FCSTD DOCUMENT  (FreeCAD 0.20R29177 (Git))
Label: FaceAr10Portrait
License: All rights reserved
LicenseURL: http://en.wikipedia.org/wiki/All_rights_reserved
objects: Sketcher::SketchObject×1, PartDesign::Body×1
note: 2 computed .brp shape members not serialized (recipe doc carries the construction recipe); baked Part::Feature solids carry a one-line shape summary decoded from their .brp
EXTERNAL_REF file=DonneesBoitier.FCStd obj=Spreadsheet

FEATURE [Sketcher::SketchObject] Sketch
  FullyConstrained = true
  MapMode = 5
  Support = -> [XY_Plane]
  expr: Constraints[108] = <<DonneesBoitier>>#<<Spreadsheet>>.xxLargeurDecoupe
  expr: Constraints[109] = <<DonneesBoitier>>#<<Spreadsheet>>.xxLongeurDecoupe
  expr: Constraints[122] = <<DonneesBoitier>>#<<Spreadsheet>>.xxEspaceDecoupe
  expr: Constraints[144] = <<DonneesBoitier>>#<<Spreadsheet>>.xxEspaceDecoupe
  expr: Constraints[1572] = <<DonneesBoitier>>#<<Spreadsheet>>.xxSautLigneDecoupe
  expr: Constraints[158] = <<DonneesBoitier>>#<<Spreadsheet>>.xxEspaceDecoupe
  expr: Constraints[206] = <<DonneesBoitier>>#<<Spreadsheet>>.xxSautLigneDecoupe
  expr: Constraints[218] = <<DonneesBoitier>>#<<Spreadsheet>>.xxEspaceDecoupe
  expr: Constraints[22] = <<DonneesBoitier>>#<<Spreadsheet>>.xxHautEncocheFemelle
  expr: Constraints[32] = <<DonneesBoitier>>#<<Spreadsheet>>.xxDiametreTrou
  expr: Constraints[336] = <<DonneesBoitier>>#<<Spreadsheet>>.xxSautLigneDecoupe
  expr: Constraints[41] = <<DonneesBoitier>>#<<Spreadsheet>>.xxLargEncocheFemelle
  expr: Constraints[42] = <<DonneesBoitier>>#<<Spreadsheet>>.xxHautEncocheFemelle
  expr: Constraints[43] = <<DonneesBoitier>>#<<Spreadsheet>>.xxLargeurEncasEcran / 4 - <<DonneesBoitier>>#<<Spreadsheet>>.xxLargEconche / 2
  expr: Constraints[52] = <<DonneesBoitier>>#<<Spreadsheet>>.xxLargEncocheFemelle
  expr: Constraints[53] = <<DonneesBoitier>>#<<Spreadsheet>>.xxHautEncocheFemelle
  expr: Constraints[578] = <<DonneesBoitier>>#<<Spreadsheet>>.xxSautLigneDecoupe
  expr: Constraints[57] = <<DonneesBoitier>>#<<Spreadsheet>>.xxEspaceDebutCourbe
  expr: Constraints[58] = <<DonneesBoitier>>#<<Spreadsheet>>.xxEspaceFinCourbe
  expr: Constraints[64] = <<DonneesBoitier>>#<<Spreadsheet>>.xxFaEspaceHaut / 2
  expr: Constraints[6] = <<DonneesBoitier>>#<<Spreadsheet>>.xxlargeur
  expr: Constraints[77] = <<DonneesBoitier>>#<<Spreadsheet>>.xxAxeEncochesFaceAv
  expr: Constraints[7] = <<DonneesBoitier>>#<<Spreadsheet>>.xxHauteurAr
  expr: Constraints[89] = <<DonneesBoitier>>#Spreadsheet.xxHauteurEncasEcran / 2 + <<DonneesBoitier>>#Spreadsheet.xxFaEspaceHaut
  expr: Constraints[937] = <<DonneesBoitier>>#<<Spreadsheet>>.xxSautLigneDecoupe
  sketch-geometry (535):
    g0: LineSegment StartX=110 StartY=-171.2 StartZ=0 EndX=110 EndY=171.2 EndZ=0
    g1: LineSegment StartX=110 StartY=171.2 StartZ=0 EndX=-110 EndY=171.2 EndZ=0
    g2: LineSegment StartX=-110 StartY=171.2 StartZ=0 EndX=-110 EndY=-171.2 EndZ=0
    g3: LineSegment StartX=-110 StartY=-171.2 StartZ=0 EndX=110 EndY=-171.2 EndZ=0
    g4: LineSegment StartX=97.3 StartY=34.7 StartZ=0 EndX=102.5 EndY=34.7 EndZ=0
    g5: LineSegment StartX=102.5 StartY=34.7 StartZ=0 EndX=102.5 EndY=19.7 EndZ=0
    g6: LineSegment StartX=102.5 StartY=19.7 StartZ=0 EndX=97.3 EndY=19.7 EndZ=0
    g7: LineSegment StartX=97.3 StartY=19.7 StartZ=0 EndX=97.3 EndY=34.7 EndZ=0
    g8: LineSegment StartX=-102.6 StartY=34.7 StartZ=0 EndX=-97.4 EndY=34.7 EndZ=0
    g9: LineSegment StartX=-97.4 StartY=34.7 StartZ=0 EndX=-97.4 EndY=19.7 EndZ=0
    g10: LineSegment StartX=-97.4 StartY=19.7 StartZ=0 EndX=-102.6 EndY=19.7 EndZ=0
    g11: LineSegment StartX=-102.6 StartY=19.7 StartZ=0 EndX=-102.6 EndY=34.7 EndZ=0
    g12: LineSegment StartX=-102.6 StartY=-10.3 StartZ=0 EndX=-97.4 EndY=-10.3 EndZ=0
    g13: LineSegment StartX=-97.4 StartY=-10.3 StartZ=0 EndX=-97.4 EndY=-25.3 EndZ=0
    g14: LineSegment StartX=-97.4 StartY=-25.3 StartZ=0 EndX=-102.6 EndY=-25.3 EndZ=0
    g15: LineSegment StartX=-102.6 StartY=-25.3 StartZ=0 EndX=-102.6 EndY=-10.3 EndZ=0
    g16: LineSegment StartX=97.3 StartY=-10.3 StartZ=0 EndX=102.5 EndY=-10.3 EndZ=0
    g17: LineSegment StartX=102.5 StartY=-10.3 StartZ=0 EndX=102.5 EndY=-25.3 EndZ=0
    g18: LineSegment StartX=102.5 StartY=-25.3 StartZ=0 EndX=97.3 EndY=-25.3 EndZ=0
    g19: LineSegment StartX=97.3 StartY=-25.3 StartZ=0 EndX=97.3 EndY=-10.3 EndZ=0
    g20: Circle CenterX=0 CenterY=153.7 CenterZ=0 NormalX=0 NormalY=0 NormalZ=1 AngleXU=0 Radius=2.625
    g21: LineSegment StartX=-53.2 StartY=156.3 StartZ=0 EndX=-38 EndY=156.3 EndZ=0
    g22: LineSegment StartX=-38 StartY=156.3 StartZ=0 EndX=-38 EndY=151.1 EndZ=0
    g23: LineSegment StartX=-38 StartY=151.1 StartZ=0 EndX=-53.2 EndY=151.1 EndZ=0
    g24: LineSegment StartX=-53.2 StartY=151.1 StartZ=0 EndX=-53.2 EndY=156.3 EndZ=0
    g25: LineSegment StartX=38 StartY=156.3 StartZ=0 EndX=53.2 EndY=156.3 EndZ=0
    g26: LineSegment StartX=53.2 StartY=156.3 StartZ=0 EndX=53.2 EndY=151.1 EndZ=0
    g27: LineSegment StartX=53.2 StartY=151.1 StartZ=0 EndX=38 EndY=151.1 EndZ=0
    g28: LineSegment StartX=38 StartY=151.1 StartZ=0 EndX=38 EndY=156.3 EndZ=0
    g29: LineSegment StartX=-125 StartY=-40.3 StartZ=0 EndX=125 EndY=-40.3 EndZ=0
    g30: LineSegment StartX=-125 StartY=-163.7 StartZ=0 EndX=125 EndY=-163.7 EndZ=0
    g31: Circle CenterX=-100 CenterY=4.7 CenterZ=0 NormalX=0 NormalY=0 NormalZ=1 AngleXU=0 Radius=2.625
    g32: Circle CenterX=99.9 CenterY=4.7 CenterZ=0 NormalX=0 NormalY=0 NormalZ=1 AngleXU=0 Radius=2.625
    g33: LineSegment StartX=-100 StartY=52.69 StartZ=0 EndX=-100 EndY=-40.3 EndZ=0
    g34: LineSegment StartX=99.9 StartY=47.73 StartZ=0 EndX=99.9 EndY=-40.3 EndZ=0
    g35: LineSegment StartX=-110 StartY=-40.3 StartZ=0 EndX=-80 EndY=-40.3 EndZ=0
    g36: LineSegment StartX=-80 StartY=-40.3 StartZ=0 EndX=-80 EndY=-42.3 EndZ=0
    g37: LineSegment StartX=-80 StartY=-42.3 StartZ=0 EndX=-110 EndY=-42.3 EndZ=0
    g38: LineSegment StartX=-110 StartY=-42.3 StartZ=0 EndX=-110 EndY=-40.3 EndZ=0
    g39: LineSegment StartX=-76 StartY=-40.3 StartZ=0 EndX=-46 EndY=-40.3 EndZ=0
    g40: LineSegment StartX=-46 StartY=-40.3 StartZ=0 EndX=-46 EndY=-42.3 EndZ=0
    g41: LineSegment StartX=-46 StartY=-42.3 StartZ=0 EndX=-76 EndY=-42.3 EndZ=0
    g42: LineSegment StartX=-76 StartY=-42.3 StartZ=0 EndX=-76 EndY=-40.3 EndZ=0
    g43: LineSegment StartX=-42 StartY=-40.3 StartZ=0 EndX=-12 EndY=-40.3 EndZ=0
    g44: LineSegment StartX=-12 StartY=-40.3 StartZ=0 EndX=-12 EndY=-42.3 EndZ=0
    g45: LineSegment StartX=-12 StartY=-42.3 StartZ=0 EndX=-42 EndY=-42.3 EndZ=0
    g46: LineSegment StartX=-42 StartY=-42.3 StartZ=0 EndX=-42 EndY=-40.3 EndZ=0
    g47: LineSegment StartX=-8 StartY=-40.3 StartZ=0 EndX=22 EndY=-40.3 EndZ=0
    g48: LineSegment StartX=22 StartY=-40.3 StartZ=0 EndX=22 EndY=-42.3 EndZ=0
    g49: LineSegment StartX=22 StartY=-42.3 StartZ=0 EndX=-8 EndY=-42.3 EndZ=0
    g50: LineSegment StartX=-8 StartY=-42.3 StartZ=0 EndX=-8 EndY=-40.3 EndZ=0
    g51: LineSegment StartX=110 StartY=-40.3 StartZ=0 EndX=26 EndY=-40.3 EndZ=0
    g52: LineSegment StartX=26 StartY=-40.3 StartZ=0 EndX=26 EndY=-42.3 EndZ=0
    g53: LineSegment StartX=26 StartY=-42.3 StartZ=0 EndX=110 EndY=-42.3 EndZ=0
    g54: LineSegment StartX=110 StartY=-42.3 StartZ=0 EndX=110 EndY=-40.3 EndZ=0
    g55: LineSegment StartX=-22 StartY=-45.3 StartZ=0 EndX=8 EndY=-45.3 EndZ=0
    g56: LineSegment StartX=8 StartY=-45.3 StartZ=0 EndX=8 EndY=-47.3 EndZ=0
    g57: LineSegment StartX=8 StartY=-47.3 StartZ=0 EndX=-22 EndY=-47.3 EndZ=0
    g58: LineSegment StartX=-22 StartY=-47.3 StartZ=0 EndX=-22 EndY=-45.3 EndZ=0
    g59: LineSegment StartX=12 StartY=-45.3 StartZ=0 EndX=42 EndY=-45.3 EndZ=0
    g60: LineSegment StartX=42 StartY=-45.3 StartZ=0 EndX=42 EndY=-47.3 EndZ=0
    g61: LineSegment StartX=42 StartY=-47.3 StartZ=0 EndX=12 EndY=-47.3 EndZ=0
    g62: LineSegment StartX=12 StartY=-47.3 StartZ=0 EndX=12 EndY=-45.3 EndZ=0
    g63: LineSegment StartX=46 StartY=-45.3 StartZ=0 EndX=76 EndY=-45.3 EndZ=0
    g64: LineSegment StartX=76 StartY=-45.3 StartZ=0 EndX=76 EndY=-47.3 EndZ=0
    g65: LineSegment StartX=76 StartY=-47.3 StartZ=0 EndX=46 EndY=-47.3 EndZ=0
    g66: LineSegment StartX=46 StartY=-47.3 StartZ=0 EndX=46 EndY=-45.3 EndZ=0
    g67: LineSegment StartX=80 StartY=-45.3 StartZ=0 EndX=110 EndY=-45.3 EndZ=0
    g68: LineSegment StartX=110 StartY=-45.3 StartZ=0 EndX=110 EndY=-47.3 EndZ=0
    g69: LineSegment StartX=110 StartY=-47.3 StartZ=0 EndX=80 EndY=-47.3 EndZ=0
    g70: LineSegment StartX=80 StartY=-47.3 StartZ=0 EndX=80 EndY=-45.3 EndZ=0
    g71: LineSegment StartX=-110 StartY=-45.3 StartZ=0 EndX=-26 EndY=-45.3 EndZ=0
    g72: LineSegment StartX=-26 StartY=-45.3 StartZ=0 EndX=-26 EndY=-47.3 EndZ=0
    g73: LineSegment StartX=-26 StartY=-47.3 StartZ=0 EndX=-110 EndY=-47.3 EndZ=0
    g74: LineSegment StartX=-110 StartY=-47.3 StartZ=0 EndX=-110 EndY=-45.3 EndZ=0
    g75: LineSegment StartX=-110 StartY=-50.3 StartZ=0 EndX=-80 EndY=-50.3 EndZ=0
    g76: LineSegment StartX=-80 StartY=-50.3 StartZ=0 EndX=-80 EndY=-52.3 EndZ=0
    g77: LineSegment StartX=-80 StartY=-52.3 StartZ=0 EndX=-110 EndY=-52.3 EndZ=0
    g78: LineSegment StartX=-110 StartY=-52.3 StartZ=0 EndX=-110 EndY=-50.3 EndZ=0
    g79: LineSegment StartX=-76 StartY=-50.3 StartZ=0 EndX=-46 EndY=-50.3 EndZ=0
    g80: LineSegment StartX=-46 StartY=-50.3 StartZ=0 EndX=-46 EndY=-52.3 EndZ=0
    g81: LineSegment StartX=-46 StartY=-52.3 StartZ=0 EndX=-76 EndY=-52.3 EndZ=0
    g82: LineSegment StartX=-76 StartY=-52.3 StartZ=0 EndX=-76 EndY=-50.3 EndZ=0
    g83: LineSegment StartX=-42 StartY=-50.3 StartZ=0 EndX=-12 EndY=-50.3 EndZ=0
    g84: LineSegment StartX=-12 StartY=-50.3 StartZ=0 EndX=-12 EndY=-52.3 EndZ=0
    g85: LineSegment StartX=-12 StartY=-52.3 StartZ=0 EndX=-42 EndY=-52.3 EndZ=0
    g86: LineSegment StartX=-42 StartY=-52.3 StartZ=0 EndX=-42 EndY=-50.3 EndZ=0
    g87: LineSegment StartX=-8 StartY=-50.3 StartZ=0 EndX=22 EndY=-50.3 EndZ=0
    g88: LineSegment StartX=22 StartY=-50.3 StartZ=0 EndX=22 EndY=-52.3 EndZ=0
    g89: LineSegment StartX=22 StartY=-52.3 StartZ=0 EndX=-8 EndY=-52.3 EndZ=0
    g90: LineSegment StartX=-8 StartY=-52.3 StartZ=0 EndX=-8 EndY=-50.3 EndZ=0
    g91: LineSegment StartX=110 StartY=-50.3 StartZ=0 EndX=26 EndY=-50.3 EndZ=0
    g92: LineSegment StartX=26 StartY=-50.3 StartZ=0 EndX=26 EndY=-52.3 EndZ=0
    g93: LineSegment StartX=26 StartY=-52.3 StartZ=0 EndX=110 EndY=-52.3 EndZ=0
    g94: LineSegment StartX=110 StartY=-52.3 StartZ=0 EndX=110 EndY=-50.3 EndZ=0
    g95: LineSegment StartX=-22 StartY=-55.3 StartZ=0 EndX=8 EndY=-55.3 EndZ=0
    g96: LineSegment StartX=8 StartY=-55.3 StartZ=0 EndX=8 EndY=-57.3 EndZ=0
    g97: LineSegment StartX=8 StartY=-57.3 StartZ=0 EndX=-22 EndY=-57.3 EndZ=0
    g98: LineSegment StartX=-22 StartY=-57.3 StartZ=0 EndX=-22 EndY=-55.3 EndZ=0
    g99: LineSegment StartX=12 StartY=-55.3 StartZ=0 EndX=42 EndY=-55.3 EndZ=0
    g100: LineSegment StartX=42 StartY=-55.3 StartZ=0 EndX=42 EndY=-57.3 EndZ=0
    g101: LineSegment StartX=42 StartY=-57.3 StartZ=0 EndX=12 EndY=-57.3 EndZ=0
    g102: LineSegment StartX=12 StartY=-57.3 StartZ=0 EndX=12 EndY=-55.3 EndZ=0
    g103: LineSegment StartX=46 StartY=-55.3 StartZ=0 EndX=76 EndY=-55.3 EndZ=0
    g104: LineSegment StartX=76 StartY=-55.3 StartZ=0 EndX=76 EndY=-57.3 EndZ=0
    g105: LineSegment StartX=76 StartY=-57.3 StartZ=0 EndX=46 EndY=-57.3 EndZ=0
    g106: LineSegment StartX=46 StartY=-57.3 StartZ=0 EndX=46 EndY=-55.3 EndZ=0
    g107: LineSegment StartX=80 StartY=-55.3 StartZ=0 EndX=110 EndY=-55.3 EndZ=0
    g108: LineSegment StartX=110 StartY=-55.3 StartZ=0 EndX=110 EndY=-57.3 EndZ=0
    g109: LineSegment StartX=110 StartY=-57.3 StartZ=0 EndX=80 EndY=-57.3 EndZ=0
    g110: LineSegment StartX=80 StartY=-57.3 StartZ=0 EndX=80 EndY=-55.3 EndZ=0
    g111: LineSegment StartX=-110 StartY=-55.3 StartZ=0 EndX=-26 EndY=-55.3 EndZ=0
    g112: LineSegment StartX=-26 StartY=-55.3 StartZ=0 EndX=-26 EndY=-57.3 EndZ=0
    g113: LineSegment StartX=-26 StartY=-57.3 StartZ=0 EndX=-110 EndY=-57.3 EndZ=0
    g114: LineSegment StartX=-110 StartY=-57.3 StartZ=0 EndX=-110 EndY=-55.3 EndZ=0
    g115: LineSegment StartX=-110 StartY=-60.3 StartZ=0 EndX=-80 EndY=-60.3 EndZ=0
    g116: LineSegment StartX=-80 StartY=-60.3 StartZ=0 EndX=-80 EndY=-62.3 EndZ=0
    g117: LineSegment StartX=-80 StartY=-62.3 StartZ=0 EndX=-110 EndY=-62.3 EndZ=0
    g118: LineSegment StartX=-110 StartY=-62.3 StartZ=0 EndX=-110 EndY=-60.3 EndZ=0
    g119: LineSegment StartX=-76 StartY=-60.3 StartZ=0 EndX=-46 EndY=-60.3 EndZ=0
    g120: LineSegment StartX=-46 StartY=-60.3 StartZ=0 EndX=-46 EndY=-62.3 EndZ=0
    g121: LineSegment StartX=-46 StartY=-62.3 StartZ=0 EndX=-76 EndY=-62.3 EndZ=0
    g122: LineSegment StartX=-76 StartY=-62.3 StartZ=0 EndX=-76 EndY=-60.3 EndZ=0
    g123: LineSegment StartX=-42 StartY=-60.3 StartZ=0 EndX=-12 EndY=-60.3 EndZ=0
    g124: LineSegment StartX=-12 StartY=-60.3 StartZ=0 EndX=-12 EndY=-62.3 EndZ=0
    g125: LineSegment StartX=-12 StartY=-62.3 StartZ=0 EndX=-42 EndY=-62.3 EndZ=0
    g126: LineSegment StartX=-42 StartY=-62.3 StartZ=0 EndX=-42 EndY=-60.3 EndZ=0
    g127: LineSegment StartX=-8 StartY=-60.3 StartZ=0 EndX=22 EndY=-60.3 EndZ=0
    g128: LineSegment StartX=22 StartY=-60.3 StartZ=0 EndX=22 EndY=-62.3 EndZ=0
    g129: LineSegment StartX=22 StartY=-62.3 StartZ=0 EndX=-8 EndY=-62.3 EndZ=0
    g130: LineSegment StartX=-8 StartY=-62.3 StartZ=0 EndX=-8 EndY=-60.3 EndZ=0
    g131: LineSegment StartX=110 StartY=-60.3 StartZ=0 EndX=26 EndY=-60.3 EndZ=0
    g132: LineSegment StartX=26 StartY=-60.3 StartZ=0 EndX=26 EndY=-62.3 EndZ=0
    g133: LineSegment StartX=26 StartY=-62.3 StartZ=0 EndX=110 EndY=-62.3 EndZ=0
    g134: LineSegment StartX=110 StartY=-62.3 StartZ=0 EndX=110 EndY=-60.3 EndZ=0
    g135: LineSegment StartX=-22 StartY=-65.3 StartZ=0 EndX=8 EndY=-65.3 EndZ=0
    g136: LineSegment StartX=8 StartY=-65.3 StartZ=0 EndX=8 EndY=-67.3 EndZ=0
    g137: LineSegment StartX=8 StartY=-67.3 StartZ=0 EndX=-22 EndY=-67.3 EndZ=0
    g138: LineSegment StartX=-22 StartY=-67.3 StartZ=0 EndX=-22 EndY=-65.3 EndZ=0
    g139: LineSegment StartX=12 StartY=-65.3 StartZ=0 EndX=42 EndY=-65.3 EndZ=0
    g140: LineSegment StartX=42 StartY=-65.3 StartZ=0 EndX=42 EndY=-67.3 EndZ=0
    g141: LineSegment StartX=42 StartY=-67.3 StartZ=0 EndX=12 EndY=-67.3 EndZ=0
    g142: LineSegment StartX=12 StartY=-67.3 StartZ=0 EndX=12 EndY=-65.3 EndZ=0
    g143: LineSegment StartX=46 StartY=-65.3 StartZ=0 EndX=76 EndY=-65.3 EndZ=0
    g144: LineSegment StartX=76 StartY=-65.3 StartZ=0 EndX=76 EndY=-67.3 EndZ=0
    g145: LineSegment StartX=76 StartY=-67.3 StartZ=0 EndX=46 EndY=-67.3 EndZ=0
    g146: LineSegment StartX=46 StartY=-67.3 StartZ=0 EndX=46 EndY=-65.3 EndZ=0
    g147: LineSegment StartX=80 StartY=-65.3 StartZ=0 EndX=110 EndY=-65.3 EndZ=0
    g148: LineSegment StartX=110 StartY=-65.3 StartZ=0 EndX=110 EndY=-67.3 EndZ=0
    g149: LineSegment StartX=110 StartY=-67.3 StartZ=0 EndX=80 EndY=-67.3 EndZ=0
    g150: LineSegment StartX=80 StartY=-67.3 StartZ=0 EndX=80 EndY=-65.3 EndZ=0
    g151: LineSegment StartX=-110 StartY=-65.3 StartZ=0 EndX=-26 EndY=-65.3 EndZ=0
    g152: LineSegment StartX=-26 StartY=-65.3 StartZ=0 EndX=-26 EndY=-67.3 EndZ=0
    g153: LineSegment StartX=-26 StartY=-67.3 StartZ=0 EndX=-110 EndY=-67.3 EndZ=0
    g154: LineSegment StartX=-110 StartY=-67.3 StartZ=0 EndX=-110 EndY=-65.3 EndZ=0
    g155: LineSegment StartX=-110 StartY=-70.3 StartZ=0 EndX=-80 EndY=-70.3 EndZ=0
    g156: LineSegment StartX=-80 StartY=-70.3 StartZ=0 EndX=-80 EndY=-72.3 EndZ=0
    g157: LineSegment StartX=-80 StartY=-72.3 StartZ=0 EndX=-110 EndY=-72.3 EndZ=0
    g158: LineSegment StartX=-110 StartY=-72.3 StartZ=0 EndX=-110 EndY=-70.3 EndZ=0
    g159: LineSegment StartX=-76 StartY=-70.3 StartZ=0 EndX=-46 EndY=-70.3 EndZ=0
    g160: LineSegment StartX=-46 StartY=-70.3 StartZ=0 EndX=-46 EndY=-72.3 EndZ=0
    g161: LineSegment StartX=-46 StartY=-72.3 StartZ=0 EndX=-76 EndY=-72.3 EndZ=0
    g162: LineSegment StartX=-76 StartY=-72.3 StartZ=0 EndX=-76 EndY=-70.3 EndZ=0
    g163: LineSegment StartX=-42 StartY=-70.3 StartZ=0 EndX=-12 EndY=-70.3 EndZ=0
    g164: LineSegment StartX=-12 StartY=-70.3 StartZ=0 EndX=-12 EndY=-72.3 EndZ=0
    g165: LineSegment StartX=-12 StartY=-72.3 StartZ=0 EndX=-42 EndY=-72.3 EndZ=0
    g166: LineSegment StartX=-42 StartY=-72.3 StartZ=0 EndX=-42 EndY=-70.3 EndZ=0
    g167: LineSegment StartX=-8 StartY=-70.3 StartZ=0 EndX=22 EndY=-70.3 EndZ=0
    g168: LineSegment StartX=22 StartY=-70.3 StartZ=0 EndX=22 EndY=-72.3 EndZ=0
    g169: LineSegment StartX=22 StartY=-72.3 StartZ=0 EndX=-8 EndY=-72.3 EndZ=0
    g170: LineSegment StartX=-8 StartY=-72.3 StartZ=0 EndX=-8 EndY=-70.3 EndZ=0
    g171: LineSegment StartX=110 StartY=-70.3 StartZ=0 EndX=26 EndY=-70.3 EndZ=0
    g172: LineSegment StartX=26 StartY=-70.3 StartZ=0 EndX=26 EndY=-72.3 EndZ=0
    g173: LineSegment StartX=26 StartY=-72.3 StartZ=0 EndX=110 EndY=-72.3 EndZ=0
    g174: LineSegment StartX=110 StartY=-72.3 StartZ=0 EndX=110 EndY=-70.3 EndZ=0
    g175: LineSegment StartX=-22 StartY=-75.3 StartZ=0 EndX=8 EndY=-75.3 EndZ=0
    g176: LineSegment StartX=8 StartY=-75.3 StartZ=0 EndX=8 EndY=-77.3 EndZ=0
    g177: LineSegment StartX=8 StartY=-77.3 StartZ=0 EndX=-22 EndY=-77.3 EndZ=0
    g178: LineSegment StartX=-22 StartY=-77.3 StartZ=0 EndX=-22 EndY=-75.3 EndZ=0
    g179: LineSegment StartX=12 StartY=-75.3 StartZ=0 EndX=42 EndY=-75.3 EndZ=0
    g180: LineSegment StartX=42 StartY=-75.3 StartZ=0 EndX=42 EndY=-77.3 EndZ=0
    g181: LineSegment StartX=42 StartY=-77.3 StartZ=0 EndX=12 EndY=-77.3 EndZ=0
    g182: LineSegment StartX=12 StartY=-77.3 StartZ=0 EndX=12 EndY=-75.3 EndZ=0
    g183: LineSegment StartX=46 StartY=-75.3 StartZ=0 EndX=76 EndY=-75.3 EndZ=0
    g184: LineSegment StartX=76 StartY=-75.3 StartZ=0 EndX=76 EndY=-77.3 EndZ=0
    g185: LineSegment StartX=76 StartY=-77.3 StartZ=0 EndX=46 EndY=-77.3 EndZ=0
    g186: LineSegment StartX=46 StartY=-77.3 StartZ=0 EndX=46 EndY=-75.3 EndZ=0
    g187: LineSegment StartX=80 StartY=-75.3 StartZ=0 EndX=110 EndY=-75.3 EndZ=0
    g188: LineSegment StartX=110 StartY=-75.3 StartZ=0 EndX=110 EndY=-77.3 EndZ=0
    g189: LineSegment StartX=110 StartY=-77.3 StartZ=0 EndX=80 EndY=-77.3 EndZ=0
    g190: LineSegment StartX=80 StartY=-77.3 StartZ=0 EndX=80 EndY=-75.3 EndZ=0
    g191: LineSegment StartX=-110 StartY=-75.3 StartZ=0 EndX=-26 EndY=-75.3 EndZ=0
    g192: LineSegment StartX=-26 StartY=-75.3 StartZ=0 EndX=-26 EndY=-77.3 EndZ=0
    g193: LineSegment StartX=-26 StartY=-77.3 StartZ=0 EndX=-110 EndY=-77.3 EndZ=0
    g194: LineSegment StartX=-110 StartY=-77.3 StartZ=0 EndX=-110 EndY=-75.3 EndZ=0
    g195: LineSegment StartX=-110 StartY=-80.3 StartZ=0 EndX=-80 EndY=-80.3 EndZ=0
    g196: LineSegment StartX=-80 StartY=-80.3 StartZ=0 EndX=-80 EndY=-82.3 EndZ=0
    g197: LineSegment StartX=-80 StartY=-82.3 StartZ=0 EndX=-110 EndY=-82.3 EndZ=0
    g198: LineSegment StartX=-110 StartY=-82.3 StartZ=0 EndX=-110 EndY=-80.3 EndZ=0
    g199: LineSegment StartX=-76 StartY=-80.3 StartZ=0 EndX=-46 EndY=-80.3 EndZ=0
    g200: LineSegment StartX=-46 StartY=-80.3 StartZ=0 EndX=-46 EndY=-82.3 EndZ=0
    g201: LineSegment StartX=-46 StartY=-82.3 StartZ=0 EndX=-76 EndY=-82.3 EndZ=0
    g202: LineSegment StartX=-76 StartY=-82.3 StartZ=0 EndX=-76 EndY=-80.3 EndZ=0
    g203: LineSegment StartX=-42 StartY=-80.3 StartZ=0 EndX=-12 EndY=-80.3 EndZ=0
    g204: LineSegment StartX=-12 StartY=-80.3 StartZ=0 EndX=-12 EndY=-82.3 EndZ=0
    g205: LineSegment StartX=-12 StartY=-82.3 StartZ=0 EndX=-42 EndY=-82.3 EndZ=0
    g206: LineSegment StartX=-42 StartY=-82.3 StartZ=0 EndX=-42 EndY=-80.3 EndZ=0
    g207: LineSegment StartX=-8 StartY=-80.3 StartZ=0 EndX=22 EndY=-80.3 EndZ=0
    g208: LineSegment StartX=22 StartY=-80.3 StartZ=0 EndX=22 EndY=-82.3 EndZ=0
    g209: LineSegment StartX=22 StartY=-82.3 StartZ=0 EndX=-8 EndY=-82.3 EndZ=0
    g210: LineSegment StartX=-8 StartY=-82.3 StartZ=0 EndX=-8 EndY=-80.3 EndZ=0
    g211: LineSegment StartX=110 StartY=-80.3 StartZ=0 EndX=26 EndY=-80.3 EndZ=0
    g212: LineSegment StartX=26 StartY=-80.3 StartZ=0 EndX=26 EndY=-82.3 EndZ=0
    g213: LineSegment StartX=26 StartY=-82.3 StartZ=0 EndX=110 EndY=-82.3 EndZ=0
    g214: LineSegment StartX=110 StartY=-82.3 StartZ=0 EndX=110 EndY=-80.3 EndZ=0
    g215: LineSegment StartX=-22 StartY=-85.3 StartZ=0 EndX=8 EndY=-85.3 EndZ=0
    g216: LineSegment StartX=8 StartY=-85.3 StartZ=0 EndX=8 EndY=-87.3 EndZ=0
    g217: LineSegment StartX=8 StartY=-87.3 StartZ=0 EndX=-22 EndY=-87.3 EndZ=0
    g218: LineSegment StartX=-22 StartY=-87.3 StartZ=0 EndX=-22 EndY=-85.3 EndZ=0
    g219: LineSegment StartX=12 StartY=-85.3 StartZ=0 EndX=42 EndY=-85.3 EndZ=0
    g220: LineSegment StartX=42 StartY=-85.3 StartZ=0 EndX=42 EndY=-87.3 EndZ=0
    g221: LineSegment StartX=42 StartY=-87.3 StartZ=0 EndX=12 EndY=-87.3 EndZ=0
    g222: LineSegment StartX=12 StartY=-87.3 StartZ=0 EndX=12 EndY=-85.3 EndZ=0
    g223: LineSegment StartX=46 StartY=-85.3 StartZ=0 EndX=76 EndY=-85.3 EndZ=0
    g224: LineSegment StartX=76 StartY=-85.3 StartZ=0 EndX=76 EndY=-87.3 EndZ=0
    g225: LineSegment StartX=76 StartY=-87.3 StartZ=0 EndX=46 EndY=-87.3 EndZ=0
    g226: LineSegment StartX=46 StartY=-87.3 StartZ=0 EndX=46 EndY=-85.3 EndZ=0
    g227: LineSegment StartX=80 StartY=-85.3 StartZ=0 EndX=110 EndY=-85.3 EndZ=0
    g228: LineSegment StartX=110 StartY=-85.3 StartZ=0 EndX=110 EndY=-87.3 EndZ=0
    g229: LineSegment StartX=110 StartY=-87.3 StartZ=0 EndX=80 EndY=-87.3 EndZ=0
    g230: LineSegment StartX=80 StartY=-87.3 StartZ=0 EndX=80 EndY=-85.3 EndZ=0
    g231: LineSegment StartX=-110 StartY=-85.3 StartZ=0 EndX=-26 EndY=-85.3 EndZ=0
    g232: LineSegment StartX=-26 StartY=-85.3 StartZ=0 EndX=-26 EndY=-87.3 EndZ=0
    g233: LineSegment StartX=-26 StartY=-87.3 StartZ=0 EndX=-110 EndY=-87.3 EndZ=0
    g234: LineSegment StartX=-110 StartY=-87.3 StartZ=0 EndX=-110 EndY=-85.3 EndZ=0
    g235: LineSegment StartX=-110 StartY=-90.3 StartZ=0 EndX=-80 EndY=-90.3 EndZ=0
    g236: LineSegment StartX=-80 StartY=-90.3 StartZ=0 EndX=-80 EndY=-92.3 EndZ=0
    g237: LineSegment StartX=-80 StartY=-92.3 StartZ=0 EndX=-110 EndY=-92.3 EndZ=0
    g238: LineSegment StartX=-110 StartY=-92.3 StartZ=0 EndX=-110 EndY=-90.3 EndZ=0
    g239: LineSegment StartX=-76 StartY=-90.3 StartZ=0 EndX=-46 EndY=-90.3 EndZ=0
    g240: LineSegment StartX=-46 StartY=-90.3 StartZ=0 EndX=-46 EndY=-92.3 EndZ=0
    g241: LineSegment StartX=-46 StartY=-92.3 StartZ=0 EndX=-76 EndY=-92.3 EndZ=0
    g242: LineSegment StartX=-76 StartY=-92.3 StartZ=0 EndX=-76 EndY=-90.3 EndZ=0
    g243: LineSegment StartX=-42 StartY=-90.3 StartZ=0 EndX=-12 EndY=-90.3 EndZ=0
    g244: LineSegment StartX=-12 StartY=-90.3 StartZ=0 EndX=-12 EndY=-92.3 EndZ=0
    g245: LineSegment StartX=-12 StartY=-92.3 StartZ=0 EndX=-42 EndY=-92.3 EndZ=0
    g246: LineSegment StartX=-42 StartY=-92.3 StartZ=0 EndX=-42 EndY=-90.3 EndZ=0
    g247: LineSegment StartX=-8 StartY=-90.3 StartZ=0 EndX=22 EndY=-90.3 EndZ=0
    g248: LineSegment StartX=22 StartY=-90.3 StartZ=0 EndX=22 EndY=-92.3 EndZ=0
    g249: LineSegment StartX=22 StartY=-92.3 StartZ=0 EndX=-8 EndY=-92.3 EndZ=0
    g250: LineSegment StartX=-8 StartY=-92.3 StartZ=0 EndX=-8 EndY=-90.3 EndZ=0
    g251: LineSegment StartX=110 StartY=-90.3 StartZ=0 EndX=26 EndY=-90.3 EndZ=0
    g252: LineSegment StartX=26 StartY=-90.3 StartZ=0 EndX=26 EndY=-92.3 EndZ=0
    g253: LineSegment StartX=26 StartY=-92.3 StartZ=0 EndX=110 EndY=-92.3 EndZ=0
    g254: LineSegment StartX=110 StartY=-92.3 StartZ=0 EndX=110 EndY=-90.3 EndZ=0
    g255: LineSegment StartX=-22 StartY=-95.3 StartZ=0 EndX=8 EndY=-95.3 EndZ=0
    g256: LineSegment StartX=8 StartY=-95.3 StartZ=0 EndX=8 EndY=-97.3 EndZ=0
    g257: LineSegment StartX=8 StartY=-97.3 StartZ=0 EndX=-22 EndY=-97.3 EndZ=0
    g258: LineSegment StartX=-22 StartY=-97.3 StartZ=0 EndX=-22 EndY=-95.3 EndZ=0
    g259: LineSegment StartX=12 StartY=-95.3 StartZ=0 EndX=42 EndY=-95.3 EndZ=0
    g260: LineSegment StartX=42 StartY=-95.3 StartZ=0 EndX=42 EndY=-97.3 EndZ=0
    g261: LineSegment StartX=42 StartY=-97.3 StartZ=0 EndX=12 EndY=-97.3 EndZ=0
    g262: LineSegment StartX=12 StartY=-97.3 StartZ=0 EndX=12 EndY=-95.3 EndZ=0
    g263: LineSegment StartX=46 StartY=-95.3 StartZ=0 EndX=76 EndY=-95.3 EndZ=0
    g264: LineSegment StartX=76 StartY=-95.3 StartZ=0 EndX=76 EndY=-97.3 EndZ=0
    g265: LineSegment StartX=76 StartY=-97.3 StartZ=0 EndX=46 EndY=-97.3 EndZ=0
    g266: LineSegment StartX=46 StartY=-97.3 StartZ=0 EndX=46 EndY=-95.3 EndZ=0
    g267: LineSegment StartX=80 StartY=-95.3 StartZ=0 EndX=110 EndY=-95.3 EndZ=0
    g268: LineSegment StartX=110 StartY=-95.3 StartZ=0 EndX=110 EndY=-97.3 EndZ=0
    g269: LineSegment StartX=110 StartY=-97.3 StartZ=0 EndX=80 EndY=-97.3 EndZ=0
    g270: LineSegment StartX=80 StartY=-97.3 StartZ=0 EndX=80 EndY=-95.3 EndZ=0
    g271: LineSegment StartX=-110 StartY=-95.3 StartZ=0 EndX=-26 EndY=-95.3 EndZ=0
    g272: LineSegment StartX=-26 StartY=-95.3 StartZ=0 EndX=-26 EndY=-97.3 EndZ=0
    g273: LineSegment StartX=-26 StartY=-97.3 StartZ=0 EndX=-110 EndY=-97.3 EndZ=0
    g274: LineSegment StartX=-110 StartY=-97.3 StartZ=0 EndX=-110 EndY=-95.3 EndZ=0
    g275: LineSegment StartX=-110 StartY=-100.3 StartZ=0 EndX=-80 EndY=-100.3 EndZ=0
    g276: LineSegment StartX=-80 StartY=-100.3 StartZ=0 EndX=-80 EndY=-102.3 EndZ=0
    g277: LineSegment StartX=-80 StartY=-102.3 StartZ=0 EndX=-110 EndY=-102.3 EndZ=0
    g278: LineSegment StartX=-110 StartY=-102.3 StartZ=0 EndX=-110 EndY=-100.3 EndZ=0
    g279: LineSegment StartX=-76 StartY=-100.3 StartZ=0 EndX=-46 EndY=-100.3 EndZ=0
    g280: LineSegment StartX=-46 StartY=-100.3 StartZ=0 EndX=-46 EndY=-102.3 EndZ=0
    g281: LineSegment StartX=-46 StartY=-102.3 StartZ=0 EndX=-76 EndY=-102.3 EndZ=0
    g282: LineSegment StartX=-76 StartY=-102.3 StartZ=0 EndX=-76 EndY=-100.3 EndZ=0
    g283: LineSegment StartX=-42 StartY=-100.3 StartZ=0 EndX=-12 EndY=-100.3 EndZ=0
    g284: LineSegment StartX=-12 StartY=-100.3 StartZ=0 EndX=-12 EndY=-102.3 EndZ=0
    g285: LineSegment StartX=-12 StartY=-102.3 StartZ=0 EndX=-42 EndY=-102.3 EndZ=0
    g286: LineSegment StartX=-42 StartY=-102.3 StartZ=0 EndX=-42 EndY=-100.3 EndZ=0
    g287: LineSegment StartX=-8 StartY=-100.3 StartZ=0 EndX=22 EndY=-100.3 EndZ=0
    g288: LineSegment StartX=22 StartY=-100.3 StartZ=0 EndX=22 EndY=-102.3 EndZ=0
    g289: LineSegment StartX=22 StartY=-102.3 StartZ=0 EndX=-8 EndY=-102.3 EndZ=0
    g290: LineSegment StartX=-8 StartY=-102.3 StartZ=0 EndX=-8 EndY=-100.3 EndZ=0
    g291: LineSegment StartX=110 StartY=-100.3 StartZ=0 EndX=26 EndY=-100.3 EndZ=0
    g292: LineSegment StartX=26 StartY=-100.3 StartZ=0 EndX=26 EndY=-102.3 EndZ=0
    g293: LineSegment StartX=26 StartY=-102.3 StartZ=0 EndX=110 EndY=-102.3 EndZ=0
    g294: LineSegment StartX=110 StartY=-102.3 StartZ=0 EndX=110 EndY=-100.3 EndZ=0
    g295: LineSegment StartX=-22 StartY=-105.3 StartZ=0 EndX=8 EndY=-105.3 EndZ=0
    g296: LineSegment StartX=8 StartY=-105.3 StartZ=0 EndX=8 EndY=-107.3 EndZ=0
    g297: LineSegment StartX=8 StartY=-107.3 StartZ=0 EndX=-22 EndY=-107.3 EndZ=0
    g298: LineSegment StartX=-22 StartY=-107.3 StartZ=0 EndX=-22 EndY=-105.3 EndZ=0
    g299: LineSegment StartX=12 StartY=-105.3 StartZ=0 EndX=42 EndY=-105.3 EndZ=0
    g300: LineSegment StartX=42 StartY=-105.3 StartZ=0 EndX=42 EndY=-107.3 EndZ=0
    g301: LineSegment StartX=42 StartY=-107.3 StartZ=0 EndX=12 EndY=-107.3 EndZ=0
    g302: LineSegment StartX=12 StartY=-107.3 StartZ=0 EndX=12 EndY=-105.3 EndZ=0
    g303: LineSegment StartX=46 StartY=-105.3 StartZ=0 EndX=76 EndY=-105.3 EndZ=0
    g304: LineSegment StartX=76 StartY=-105.3 StartZ=0 EndX=76 EndY=-107.3 EndZ=0
    g305: LineSegment StartX=76 StartY=-107.3 StartZ=0 EndX=46 EndY=-107.3 EndZ=0
    g306: LineSegment StartX=46 StartY=-107.3 StartZ=0 EndX=46 EndY=-105.3 EndZ=0
    g307: LineSegment StartX=80 StartY=-105.3 StartZ=0 EndX=110 EndY=-105.3 EndZ=0
    g308: LineSegment StartX=110 StartY=-105.3 StartZ=0 EndX=110 EndY=-107.3 EndZ=0
    g309: LineSegment StartX=110 StartY=-107.3 StartZ=0 EndX=80 EndY=-107.3 EndZ=0
    g310: LineSegment StartX=80 StartY=-107.3 StartZ=0 EndX=80 EndY=-105.3 EndZ=0
    g311: LineSegment StartX=-110 StartY=-105.3 StartZ=0 EndX=-26 EndY=-105.3 EndZ=0
    g312: LineSegment StartX=-26 StartY=-105.3 StartZ=0 EndX=-26 EndY=-107.3 EndZ=0
    g313: LineSegment StartX=-26 StartY=-107.3 StartZ=0 EndX=-110 EndY=-107.3 EndZ=0
    g314: LineSegment StartX=-110 StartY=-107.3 StartZ=0 EndX=-110 EndY=-105.3 EndZ=0
    g315: LineSegment StartX=-110 StartY=-110.3 StartZ=0 EndX=-80 EndY=-110.3 EndZ=0
    g316: LineSegment StartX=-80 StartY=-110.3 StartZ=0 EndX=-80 EndY=-112.3 EndZ=0
    g317: LineSegment StartX=-80 StartY=-112.3 StartZ=0 EndX=-110 EndY=-112.3 EndZ=0
    g318: LineSegment StartX=-110 StartY=-112.3 StartZ=0 EndX=-110 EndY=-110.3 EndZ=0
    g319: LineSegment StartX=-76 StartY=-110.3 StartZ=0 EndX=-46 EndY=-110.3 EndZ=0
    g320: LineSegment StartX=-46 StartY=-110.3 StartZ=0 EndX=-46 EndY=-112.3 EndZ=0
    g321: LineSegment StartX=-46 StartY=-112.3 StartZ=0 EndX=-76 EndY=-112.3 EndZ=0
    g322: LineSegment StartX=-76 StartY=-112.3 StartZ=0 EndX=-76 EndY=-110.3 EndZ=0
    g323: LineSegment StartX=-42 StartY=-110.3 StartZ=0 EndX=-12 EndY=-110.3 EndZ=0
    g324: LineSegment StartX=-12 StartY=-110.3 StartZ=0 EndX=-12 EndY=-112.3 EndZ=0
    g325: LineSegment StartX=-12 StartY=-112.3 StartZ=0 EndX=-42 EndY=-112.3 EndZ=0
    g326: LineSegment StartX=-42 StartY=-112.3 StartZ=0 EndX=-42 EndY=-110.3 EndZ=0
    g327: LineSegment StartX=-8 StartY=-110.3 StartZ=0 EndX=22 EndY=-110.3 EndZ=0
    g328: LineSegment StartX=22 StartY=-110.3 StartZ=0 EndX=22 EndY=-112.3 EndZ=0
    g329: LineSegment StartX=22 StartY=-112.3 StartZ=0 EndX=-8 EndY=-112.3 EndZ=0
    g330: LineSegment StartX=-8 StartY=-112.3 StartZ=0 EndX=-8 EndY=-110.3 EndZ=0
    g331: LineSegment StartX=110 StartY=-110.3 StartZ=0 EndX=26 EndY=-110.3 EndZ=0
    g332: LineSegment StartX=26 StartY=-110.3 StartZ=0 EndX=26 EndY=-112.3 EndZ=0
    g333: LineSegment StartX=26 StartY=-112.3 StartZ=0 EndX=110 EndY=-112.3 EndZ=0
    g334: LineSegment StartX=110 StartY=-112.3 StartZ=0 EndX=110 EndY=-110.3 EndZ=0
    g335: LineSegment StartX=-22 StartY=-115.3 StartZ=0 EndX=8 EndY=-115.3 EndZ=0
    g336: LineSegment StartX=8 StartY=-115.3 StartZ=0 EndX=8 EndY=-117.3 EndZ=0
    g337: LineSegment StartX=8 StartY=-117.3 StartZ=0 EndX=-22 EndY=-117.3 EndZ=0
    g338: LineSegment StartX=-22 StartY=-117.3 StartZ=0 EndX=-22 EndY=-115.3 EndZ=0
    g339: LineSegment StartX=12 StartY=-115.3 StartZ=0 EndX=42 EndY=-115.3 EndZ=0
    g340: LineSegment StartX=42 StartY=-115.3 StartZ=0 EndX=42 EndY=-117.3 EndZ=0
    g341: LineSegment StartX=42 StartY=-117.3 StartZ=0 EndX=12 EndY=-117.3 EndZ=0
    g342: LineSegment StartX=12 StartY=-117.3 StartZ=0 EndX=12 EndY=-115.3 EndZ=0
    g343: LineSegment StartX=46 StartY=-115.3 StartZ=0 EndX=76 EndY=-115.3 EndZ=0
    g344: LineSegment StartX=76 StartY=-115.3 StartZ=0 EndX=76 EndY=-117.3 EndZ=0
    g345: LineSegment StartX=76 StartY=-117.3 StartZ=0 EndX=46 EndY=-117.3 EndZ=0
    g346: LineSegment StartX=46 StartY=-117.3 StartZ=0 EndX=46 EndY=-115.3 EndZ=0
    g347: LineSegment StartX=80 StartY=-115.3 StartZ=0 EndX=110 EndY=-115.3 EndZ=0
    g348: LineSegment StartX=110 StartY=-115.3 StartZ=0 EndX=110 EndY=-117.3 EndZ=0
    g349: LineSegment StartX=110 StartY=-117.3 StartZ=0 EndX=80 EndY=-117.3 EndZ=0
    g350: LineSegment StartX=80 StartY=-117.3 StartZ=0 EndX=80 EndY=-115.3 EndZ=0
    g351: LineSegment StartX=-110 StartY=-115.3 StartZ=0 EndX=-26 EndY=-115.3 EndZ=0
    g352: LineSegment StartX=-26 StartY=-115.3 StartZ=0 EndX=-26 EndY=-117.3 EndZ=0
    g353: LineSegment StartX=-26 StartY=-117.3 StartZ=0 EndX=-110 EndY=-117.3 EndZ=0
    g354: LineSegment StartX=-110 StartY=-117.3 StartZ=0 EndX=-110 EndY=-115.3 EndZ=0
    g355: LineSegment StartX=-110 StartY=-120.3 StartZ=0 EndX=-80 EndY=-120.3 EndZ=0
    g356: LineSegment StartX=-80 StartY=-120.3 StartZ=0 EndX=-80 EndY=-122.3 EndZ=0
    g357: LineSegment StartX=-80 StartY=-122.3 StartZ=0 EndX=-110 EndY=-122.3 EndZ=0
    g358: LineSegment StartX=-110 StartY=-122.3 StartZ=0 EndX=-110 EndY=-120.3 EndZ=0
    g359: LineSegment StartX=-76 StartY=-120.3 StartZ=0 EndX=-46 EndY=-120.3 EndZ=0
    g360: LineSegment StartX=-46 StartY=-120.3 StartZ=0 EndX=-46 EndY=-122.3 EndZ=0
    g361: LineSegment StartX=-46 StartY=-122.3 StartZ=0 EndX=-76 EndY=-122.3 EndZ=0
    g362: LineSegment StartX=-76 StartY=-122.3 StartZ=0 EndX=-76 EndY=-120.3 EndZ=0
    g363: LineSegment StartX=-42 StartY=-120.3 StartZ=0 EndX=-12 EndY=-120.3 EndZ=0
    g364: LineSegment StartX=-12 StartY=-120.3 StartZ=0 EndX=-12 EndY=-122.3 EndZ=0
    g365: LineSegment StartX=-12 StartY=-122.3 StartZ=0 EndX=-42 EndY=-122.3 EndZ=0
    g366: LineSegment StartX=-42 StartY=-122.3 StartZ=0 EndX=-42 EndY=-120.3 EndZ=0
    g367: LineSegment StartX=-8 StartY=-120.3 StartZ=0 EndX=22 EndY=-120.3 EndZ=0
    g368: LineSegment StartX=22 StartY=-120.3 StartZ=0 EndX=22 EndY=-122.3 EndZ=0
    g369: LineSegment StartX=22 StartY=-122.3 StartZ=0 EndX=-8 EndY=-122.3 EndZ=0
    g370: LineSegment StartX=-8 StartY=-122.3 StartZ=0 EndX=-8 EndY=-120.3 EndZ=0
    g371: LineSegment StartX=110 StartY=-120.3 StartZ=0 EndX=26 EndY=-120.3 EndZ=0
    g372: LineSegment StartX=26 StartY=-120.3 StartZ=0 EndX=26 EndY=-122.3 EndZ=0
    g373: LineSegment StartX=26 StartY=-122.3 StartZ=0 EndX=110 EndY=-122.3 EndZ=0
    g374: LineSegment StartX=110 StartY=-122.3 StartZ=0 EndX=110 EndY=-120.3 EndZ=0
    g375: LineSegment StartX=-22 StartY=-125.3 StartZ=0 EndX=8 EndY=-125.3 EndZ=0
    g376: LineSegment StartX=8 StartY=-125.3 StartZ=0 EndX=8 EndY=-127.3 EndZ=0
    g377: LineSegment StartX=8 StartY=-127.3 StartZ=0 EndX=-22 EndY=-127.3 EndZ=0
    g378: LineSegment StartX=-22 StartY=-127.3 StartZ=0 EndX=-22 EndY=-125.3 EndZ=0
    g379: LineSegment StartX=12 StartY=-125.3 StartZ=0 EndX=42 EndY=-125.3 EndZ=0
    g380: LineSegment StartX=42 StartY=-125.3 StartZ=0 EndX=42 EndY=-127.3 EndZ=0
    g381: LineSegment StartX=42 StartY=-127.3 StartZ=0 EndX=12 EndY=-127.3 EndZ=0
    g382: LineSegment StartX=12 StartY=-127.3 StartZ=0 EndX=12 EndY=-125.3 EndZ=0
    g383: LineSegment StartX=46 StartY=-125.3 StartZ=0 EndX=76 EndY=-125.3 EndZ=0
    g384: LineSegment StartX=76 StartY=-125.3 StartZ=0 EndX=76 EndY=-127.3 EndZ=0
    g385: LineSegment StartX=76 StartY=-127.3 StartZ=0 EndX=46 EndY=-127.3 EndZ=0
    g386: LineSegment StartX=46 StartY=-127.3 StartZ=0 EndX=46 EndY=-125.3 EndZ=0
    g387: LineSegment StartX=80 StartY=-125.3 StartZ=0 EndX=110 EndY=-125.3 EndZ=0
    g388: LineSegment StartX=110 StartY=-125.3 StartZ=0 EndX=110 EndY=-127.3 EndZ=0
    g389: LineSegment StartX=110 StartY=-127.3 StartZ=0 EndX=80 EndY=-127.3 EndZ=0
    g390: LineSegment StartX=80 StartY=-127.3 StartZ=0 EndX=80 EndY=-125.3 EndZ=0
    g391: LineSegment StartX=-110 StartY=-125.3 StartZ=0 EndX=-26 EndY=-125.3 EndZ=0
    g392: LineSegment StartX=-26 StartY=-125.3 StartZ=0 EndX=-26 EndY=-127.3 EndZ=0
    g393: LineSegment StartX=-26 StartY=-127.3 StartZ=0 EndX=-110 EndY=-127.3 EndZ=0
    g394: LineSegment StartX=-110 StartY=-127.3 StartZ=0 EndX=-110 EndY=-125.3 EndZ=0
    g395: LineSegment StartX=-110 StartY=-130.3 StartZ=0 EndX=-80 EndY=-130.3 EndZ=0
    g396: LineSegment StartX=-80 StartY=-130.3 StartZ=0 EndX=-80 EndY=-132.3 EndZ=0
    g397: LineSegment StartX=-80 StartY=-132.3 StartZ=0 EndX=-110 EndY=-132.3 EndZ=0
    g398: LineSegment StartX=-110 StartY=-132.3 StartZ=0 EndX=-110 EndY=-130.3 EndZ=0
    g399: LineSegment StartX=-76 StartY=-130.3 StartZ=0 EndX=-46 EndY=-130.3 EndZ=0
    ... +135 more geometry lines
  constraints (1599):
    c: Coincident(g0,g1)
    c: Coincident(g1,g2)
    c: Coincident(g2,g3)
    c: Coincident(g3,g0)
    c: Horizontal(g3)
    c: Vertical(g0)
    c: DistanceX(g1,g0) = 220
    c: DistanceY(g2,g1) = 342.4
    c: Symmetric(g1,g0,g-2)
    c: Symmetric(g1,g2,g-1)
    c: Horizontal(g4)
    c: Horizontal(g6)
    c: Vertical(g5)
    c: Vertical(g7)
    c: Coincident(g8,g9)
    c: Coincident(g9,g10)
    c: Coincident(g10,g11)
    c: Coincident(g11,g8)
    c: Horizontal(g8)
    c: Horizontal(g10)
    c: Vertical(g9)
    c: Vertical(g11)
    c: DistanceX(g8,g8) = 5.2
    c: DistanceY(g9,g8) = 15
    c: Horizontal(g12)
    c: Horizontal(g14)
    c: Vertical(g13)
    c: Vertical(g15)
    c: Horizontal(g18)
    c: Vertical(g17)
    c: Vertical(g19)
    c: PointOnObject(g20,g-2)
    c: Diameter(g20) = 5.25
    c: Coincident(g21,g22)
    c: Coincident(g22,g23)
    c: Coincident(g23,g24)
    c: Coincident(g24,g21)
    c: Horizontal(g21)
    c: Horizontal(g23)
    c: Vertical(g22)
    c: Vertical(g24)
    c: DistanceX(g21,g21) = 15.2
    c: DistanceY(g22,g21) = 5.2
    c: DistanceX(g21,g20) = 38
    c: Coincident(g25,g26)
    c: Coincident(g26,g27)
    c: Coincident(g27,g28)
    c: Coincident(g28,g25)
    c: Horizontal(g25)
    c: Horizontal(g27)
    c: Vertical(g26)
    c: Vertical(g28)
    c: DistanceX(g25,g25) = 15.2
    c: DistanceY(g26,g25) = 5.2
    c: Symmetric(g22,g27,g-2)
    c: DistanceX(g29,g29) = 250
    c: Equal(g29,g30)
    c: DistanceY(g29,g14) = 15
    c: DistanceY(g2,g30) = 7.5
    c: Symmetric(g30,g30,g-2)
    c: Symmetric(g29,g29,g-2)
    c: Symmetric(g9,g12,g31)
    c: Diameter(g32) = 5.25
    c: Symmetric(g16,g5,g32)
    c: DistanceY(g20,g1) = 17.5
    c: Equal(g8,g4)
    c: Equal(g4,g16)
    c: Equal(g16,g12)
    c: Equal(g11,g7)
    c: Equal(g7,g19)
    c: Equal(g19,g15)
    c: Coincident(g15,g12)
    c: Coincident(g14,g15)
    c: Coincident(g13,g14)
    c: Coincident(g13,g12)
    c: Distance(g33) = 92.99
    c: Distance(g34) = 88.03
    c: DistanceX(g1,g33) = 10
    c: Symmetric(g8,g8,g33)
    c: PointOnObject(g31,g33)
    c: DistanceY(g31,g10) = 15
    c: Coincident(g7,g6)
    c: Coincident(g4,g7)
    c: Symmetric(g6,g5,g34)
    c: Coincident(g17,g16)
    c: Coincident(g19,g16)
    c: Coincident(g18,g19)
    c: Coincident(g17,g18)
    c: Symmetric(g16,g16,g34)
    c: DistanceY(g31,g1) = 166.5
    c: DistanceY(g32,g31) = 0
    c: DistanceY(g20,g25) = 2.6
    c: DistanceY(g4,g8) = 0
    c: Coincident(g5,g4)
    c: Coincident(g6,g5)
    c: DistanceX(g32,g0) = 10.1
    c: PointOnObject(g33,g29)
    c: PointOnObject(g34,g29)
    c: Equal(g31,g32)
    c: Coincident(g35,g36)
    c: Coincident(g36,g37)
    c: Coincident(g37,g38)
    c: Coincident(g38,g35)
    c: Horizontal(g35)
    c: Horizontal(g37)
    c: Vertical(g36)
    c: Vertical(g38)
    c: PointOnObject(g35,g2)
    c: Distance(g36) = 2
    c: Distance(g35) = 30
    c: DistanceY(g35,g33) = 0
    c: Coincident(g39,g40)
    c: Coincident(g40,g41)
    c: Coincident(g41,g42)
    c: Coincident(g42,g39)
    c: Horizontal(g39)
    c: Horizontal(g41)
    c: Vertical(g40)
    c: Vertical(g42)
    c: PointOnObject(g39,g29)
    c: Equal(g36,g42)
    c: Equal(g35,g39)
    c: DistanceX(g35,g39) = 4
    c: Coincident(g43,g44)
    c: Coincident(g44,g45)
    c: Coincident(g45,g46)
    c: Coincident(g46,g43)
    c: Horizontal(g43)
    c: Horizontal(g45)
    c: Vertical(g44)
    c: Vertical(g46)
    c: Equal(g36,g44) = 2
    c: Equal(g35,g43) = 30
    c: Coincident(g47,g48)
    c: Coincident(g48,g49)
    c: Coincident(g49,g50)
    c: Coincident(g50,g47)
    c: Horizontal(g47)
    c: Horizontal(g49)
    c: Vertical(g48)
    c: Vertical(g50)
    c: Equal(g44,g50)
    c: Equal(g43,g47)
    c: DistanceX(g43,g47) = 4
    c: DistanceX(g39,g43) = 4
    c: PointOnObject(g43,g29)
    c: PointOnObject(g47,g29)
    c: Coincident(g51,g52)
    c: Coincident(g52,g53)
    c: Coincident(g53,g54)
    c: Coincident(g54,g51)
    c: Horizontal(g51)
    c: Horizontal(g53)
    c: Vertical(g52)
    c: Vertical(g54)
    c: PointOnObject(g51,g0)
    c: PointOnObject(g51,g29)
    c: Equal(g48,g52)
    c: DistanceX(g47,g51) = 4
    c: Coincident(g55,g56)
    c: Coincident(g56,g57)
    c: Coincident(g57,g58)
    c: Coincident(g58,g55)
    c: Horizontal(g55)
    c: Horizontal(g57)
    c: Vertical(g56)
    c: Vertical(g58)
    c: Equal(g36,g56) = 2
    c: Equal(g35,g55) = 30
    c: Coincident(g59,g60)
    c: Coincident(g60,g61)
    c: Coincident(g61,g62)
    c: Coincident(g62,g59)
    c: Horizontal(g59)
    c: Horizontal(g61)
    c: Vertical(g60)
    c: Vertical(g62)
    c: Equal(g56,g62)
    c: Equal(g55,g59)
    c: DistanceX(g55,g59) = 4
    c: Coincident(g63,g64)
    c: Coincident(g64,g65)
    c: Coincident(g65,g66)
    c: Coincident(g66,g63)
    c: Horizontal(g63)
    c: Horizontal(g65)
    c: Vertical(g64)
    c: Vertical(g66)
    c: Equal(g56,g64) = 2
    c: Equal(g55,g63) = 30
    c: Coincident(g67,g68)
    c: Coincident(g68,g69)
    c: Coincident(g69,g70)
    c: Coincident(g70,g67)
    c: Horizontal(g67)
    c: Horizontal(g69)
    c: Vertical(g68)
    c: Vertical(g70)
    c: Equal(g64,g70)
    c: Equal(g63,g67)
    c: DistanceX(g63,g67) = 4
    c: DistanceX(g59,g63) = 4
    c: DistanceY(g63,g67) = 0
    c: DistanceY(g63,g59) = 0
    c: DistanceY(g59,g55) = 0
    c: PointOnObject(g67,g0)
    c: DistanceY(g67,g48) = 3
    c: Coincident(g71,g72)
    c: Coincident(g72,g73)
    c: Coincident(g73,g74)
    c: Coincident(g74,g71)
    c: Horizontal(g71)
    c: Horizontal(g73)
    c: Vertical(g72)
    c: Vertical(g74)
    c: PointOnObject(g71,g2)
    c: Equal(g58,g72)
    c: DistanceY(g71,g55) = 0
    c: DistanceX(g72,g57) = 4
    c: Coincident(g75,g76)
    c: Coincident(g76,g77)
    c: Coincident(g77,g78)
    c: Coincident(g78,g75)
    c: Horizontal(g75)
    c: Horizontal(g77)
    c: Vertical(g76)
    c: Vertical(g78)
    c: Equal(g36,g76) = 2
    c: Equal(g35,g75) = 30
    c: Coincident(g79,g80)
    c: Coincident(g80,g81)
    c: Coincident(g81,g82)
    c: Coincident(g82,g79)
    c: Horizontal(g79)
    c: Horizontal(g81)
    c: Vertical(g80)
    c: Vertical(g82)
    c: Equal(g76,g82)
    c: Equal(g75,g79)
    c: DistanceX(g75,g79) = 4
    c: Coincident(g83,g84)
    c: Coincident(g84,g85)
    c: Coincident(g85,g86)
    c: Coincident(g86,g83)
    c: Horizontal(g83)
    c: Horizontal(g85)
    c: Vertical(g84)
    c: Vertical(g86)
    c: Equal(g76,g84) = 2
    c: Equal(g75,g83) = 30
    c: Coincident(g87,g88)
    c: Coincident(g88,g89)
    c: Coincident(g89,g90)
    c: Coincident(g90,g87)
    c: Horizontal(g87)
    c: Horizontal(g89)
    c: Vertical(g88)
    c: Vertical(g90)
    c: Equal(g84,g90)
    c: Equal(g83,g87)
    c: DistanceX(g83,g87) = 4
    c: DistanceX(g79,g83) = 4
    c: Coincident(g91,g92)
    c: Coincident(g92,g93)
    c: Coincident(g93,g94)
    c: Coincident(g94,g91)
    c: Horizontal(g91)
    c: Horizontal(g93)
    c: Vertical(g92)
    c: Vertical(g94)
    c: Equal(g88,g92)
    c: DistanceX(g87,g91) = 4
    c: Coincident(g95,g96)
    c: Coincident(g96,g97)
    c: Coincident(g97,g98)
    c: Coincident(g98,g95)
    c: Horizontal(g95)
    c: Horizontal(g97)
    c: Vertical(g96)
    c: Vertical(g98)
    c: Equal(g76,g96) = 2
    c: Equal(g75,g95) = 30
    c: Coincident(g99,g100)
    c: Coincident(g100,g101)
    c: Coincident(g101,g102)
    c: Coincident(g102,g99)
    c: Horizontal(g99)
    c: Horizontal(g101)
    c: Vertical(g100)
    c: Vertical(g102)
    c: Equal(g96,g102)
    c: Equal(g95,g99)
    c: DistanceX(g95,g99) = 4
    c: Coincident(g103,g104)
    c: Coincident(g104,g105)
    c: Coincident(g105,g106)
    c: Coincident(g106,g103)
    c: Horizontal(g103)
    c: Horizontal(g105)
    c: Vertical(g104)
    c: Vertical(g106)
    c: Equal(g96,g104) = 2
    c: Equal(g95,g103) = 30
    c: Coincident(g107,g108)
    c: Coincident(g108,g109)
    c: Coincident(g109,g110)
    c: Coincident(g110,g107)
    c: Horizontal(g107)
    c: Horizontal(g109)
    c: Vertical(g108)
    c: Vertical(g110)
    c: Equal(g104,g110)
    c: Equal(g103,g107)
    c: DistanceX(g103,g107) = 4
    c: DistanceX(g99,g103) = 4
    c: DistanceY(g103,g107) = 0
    c: DistanceY(g103,g99) = 0
    c: DistanceY(g99,g95) = 0
    c: DistanceY(g107,g88) = 3
    c: Coincident(g111,g112)
    c: Coincident(g112,g113)
    c: Coincident(g113,g114)
    c: Coincident(g114,g111)
    c: Horizontal(g111)
    c: Horizontal(g113)
    c: Vertical(g112)
    c: Vertical(g114)
    c: Equal(g98,g112)
    c: DistanceY(g111,g95) = 0
    c: DistanceX(g112,g97) = 4
    c: PointOnObject(g114,g2)
    c: DistanceY(g75,g79) = 0
    c: DistanceY(g79,g83) = 0
    c: DistanceY(g83,g87) = 0
    c: DistanceY(g87,g91) = 0
    c: PointOnObject(g75,g2)
    c: DistanceY(g75,g73) = 3
    c: PointOnObject(g107,g0)
    c: PointOnObject(g91,g0)
    c: Coincident(g115,g116)
    c: Coincident(g116,g117)
    c: Coincident(g117,g118)
    c: Coincident(g118,g115)
    c: Horizontal(g115)
    c: Horizontal(g117)
    c: Vertical(g116)
    c: Vertical(g118)
    c: Equal(g36,g116) = 2
    c: Equal(g35,g115) = 30
    c: Coincident(g119,g120)
    c: Coincident(g120,g121)
    c: Coincident(g121,g122)
    c: Coincident(g122,g119)
    c: Horizontal(g119)
    c: Horizontal(g121)
    c: Vertical(g120)
    c: Vertical(g122)
    c: Equal(g116,g122)
    c: Equal(g115,g119)
    c: DistanceX(g115,g119) = 4
    c: Coincident(g123,g124)
    c: Coincident(g124,g125)
    c: Coincident(g125,g126)
    c: Coincident(g126,g123)
    c: Horizontal(g123)
    c: Horizontal(g125)
    c: Vertical(g124)
    c: Vertical(g126)
    c: Equal(g116,g124) = 2
    c: Equal(g115,g123) = 30
    c: Coincident(g127,g128)
    c: Coincident(g128,g129)
    c: Coincident(g129,g130)
    c: Coincident(g130,g127)
    c: Horizontal(g127)
    c: Horizontal(g129)
    c: Vertical(g128)
    c: Vertical(g130)
    c: Equal(g124,g130)
    c: Equal(g123,g127)
    c: DistanceX(g123,g127) = 4
    c: DistanceX(g119,g123) = 4
    c: Coincident(g131,g132)
    c: Coincident(g132,g133)
    c: Coincident(g133,g134)
    c: Coincident(g134,g131)
    c: Horizontal(g131)
    c: Horizontal(g133)
    c: Vertical(g132)
    c: Vertical(g134)
    c: Equal(g128,g132)
    c: DistanceX(g127,g131) = 4
    c: Coincident(g135,g136)
    c: Coincident(g136,g137)
    c: Coincident(g137,g138)
    c: Coincident(g138,g135)
    c: Horizontal(g135)
    c: Horizontal(g137)
    c: Vertical(g136)
    c: Vertical(g138)
    c: Equal(g116,g136) = 2
    c: Equal(g115,g135) = 30
    c: Coincident(g139,g140)
    c: Coincident(g140,g141)
    c: Coincident(g141,g142)
    c: Coincident(g142,g139)
    c: Horizontal(g139)
    c: Horizontal(g141)
    c: Vertical(g140)
    c: Vertical(g142)
    c: Equal(g136,g142)
    c: Equal(g135,g139)
    c: DistanceX(g135,g139) = 4
    c: Coincident(g143,g144)
    c: Coincident(g144,g145)
    c: Coincident(g145,g146)
    c: Coincident(g146,g143)
    c: Horizontal(g143)
    c: Horizontal(g145)
    c: Vertical(g144)
    c: Vertical(g146)
    c: Equal(g136,g144) = 2
    c: Equal(g135,g143) = 30
    c: Coincident(g147,g148)
    c: Coincident(g148,g149)
    c: Coincident(g149,g150)
    c: Coincident(g150,g147)
    c: Horizontal(g147)
    c: Horizontal(g149)
    c: Vertical(g148)
    c: Vertical(g150)
    c: Equal(g144,g150)
    c: Equal(g143,g147)
    c: DistanceX(g143,g147) = 4
    c: DistanceX(g139,g143) = 4
    c: DistanceY(g143,g147) = 0
    c: DistanceY(g143,g139) = 0
    c: DistanceY(g139,g135) = 0
    c: DistanceY(g147,g128) = 3
    c: Coincident(g151,g152)
    c: Coincident(g152,g153)
    c: Coincident(g153,g154)
    c: Coincident(g154,g151)
    c: Horizontal(g151)
    c: Horizontal(g153)
    c: Vertical(g152)
    c: Vertical(g154)
    c: Equal(g138,g152)
    c: DistanceY(g151,g135) = 0
    c: DistanceX(g152,g137) = 4
    c: Coincident(g155,g156)
    c: Coincident(g156,g157)
    c: Coincident(g157,g158)
    c: Coincident(g158,g155)
    c: Horizontal(g155)
    c: Horizontal(g157)
    c: Vertical(g156)
    c: Vertical(g158)
    c: Equal(g116,g156) = 2
    c: Equal(g115,g155) = 30
    c: Coincident(g159,g160)
    c: Coincident(g160,g161)
    c: Coincident(g161,g162)
    c: Coincident(g162,g159)
    c: Horizontal(g159)
    c: Horizontal(g161)
    c: Vertical(g160)
    c: Vertical(g162)
    c: Equal(g156,g162)
    c: Equal(g155,g159)
    c: DistanceX(g155,g159) = 4
    c: Coincident(g163,g164)
    c: Coincident(g164,g165)
    c: Coincident(g165,g166)
    c: Coincident(g166,g163)
    c: Horizontal(g163)
    c: Horizontal(g165)
    c: Vertical(g164)
    c: Vertical(g166)
    c: Equal(g156,g164) = 2
    c: Equal(g155,g163) = 30
    c: Coincident(g167,g168)
    c: Coincident(g168,g169)
    c: Coincident(g169,g170)
    c: Coincident(g170,g167)
    c: Horizontal(g167)
    c: Horizontal(g169)
    c: Vertical(g168)
    c: Vertical(g170)
    c: Equal(g164,g170)
    c: Equal(g163,g167)
    c: DistanceX(g163,g167) = 4
    c: DistanceX(g159,g163) = 4
    c: Coincident(g171,g172)
    c: Coincident(g172,g173)
    c: Coincident(g173,g174)
    c: Coincident(g174,g171)
    c: Horizontal(g171)
    c: Horizontal(g173)
    c: Vertical(g172)
    c: Vertical(g174)
    c: Equal(g168,g172)
    c: DistanceX(g167,g171) = 4
    c: Coincident(g175,g176)
    c: Coincident(g176,g177)
    c: Coincident(g177,g178)
    c: Coincident(g178,g175)
    c: Horizontal(g175)
    c: Horizontal(g177)
    c: Vertical(g176)
    c: Vertical(g178)
    c: Equal(g156,g176) = 2
    c: Equal(g155,g175) = 30
    c: Coincident(g179,g180)
    c: Coincident(g180,g181)
    c: Coincident(g181,g182)
    c: Coincident(g182,g179)
    c: Horizontal(g179)
    c: Horizontal(g181)
    c: Vertical(g180)
    c: Vertical(g182)
    c: Equal(g176,g182)
    c: Equal(g175,g179)
    c: DistanceX(g175,g179) = 4
    c: Coincident(g183,g184)
    c: Coincident(g184,g185)
    c: Coincident(g185,g186)
    c: Coincident(g186,g183)
    c: Horizontal(g183)
    c: Horizontal(g185)
    c: Vertical(g184)
    c: Vertical(g186)
    c: Equal(g176,g184) = 2
    c: Equal(g175,g183) = 30
    c: Coincident(g187,g188)
    c: Coincident(g188,g189)
    c: Coincident(g189,g190)
    c: Coincident(g190,g187)
    c: Horizontal(g187)
    c: Horizontal(g189)
    c: Vertical(g188)
    c: Vertical(g190)
    c: Equal(g184,g190)
    c: Equal(g183,g187)
    c: DistanceX(g183,g187) = 4
    c: DistanceX(g179,g183) = 4
    c: DistanceY(g183,g187) = 0
    c: DistanceY(g183,g179) = 0
    c: DistanceY(g179,g175) = 0
    c: DistanceY(g187,g168) = 3
    c: Coincident(g191,g192)
    c: Coincident(g192,g193)
    c: Coincident(g193,g194)
    c: Coincident(g194,g191)
    c: Horizontal(g191)
    c: Horizontal(g193)
    c: Vertical(g192)
    c: Vertical(g194)
    c: Equal(g178,g192)
    c: DistanceY(g191,g175) = 0
    c: DistanceX(g192,g177) = 4
    c: DistanceY(g155,g159) = 0
    c: DistanceY(g159,g163) = 0
    c: DistanceY(g163,g167) = 0
    c: DistanceY(g167,g171) = 0
    c: DistanceY(g155,g153) = 3
    c: PointOnObject(g194,g2)
    c: DistanceY(g119,g115) = 0
    c: DistanceY(g123,g119) = 0
    c: DistanceY(g127,g123) = 0
    c: DistanceY(g127,g131) = 0
    c: PointOnObject(g131,g0)
    c: PointOnObject(g147,g0)
    c: PointOnObject(g171,g0)
    c: PointOnObject(g187,g0)
    c: PointOnObject(g115,g2)
    c: PointOnObject(g151,g2)
    c: PointOnObject(g155,g2)
    c: DistanceY(g115,g113) = 3
    c: Coincident(g195,g196)
    c: Coincident(g196,g197)
    c: Coincident(g197,g198)
    c: Coincident(g198,g195)
    c: Horizontal(g195)
    c: Horizontal(g197)
    c: Vertical(g196)
    c: Vertical(g198)
    c: Coincident(g199,g200)
    c: Coincident(g200,g201)
    c: Coincident(g201,g202)
    c: Coincident(g202,g199)
    c: Horizontal(g199)
    c: Horizontal(g201)
    c: Vertical(g200)
    c: Vertical(g202)
    c: Equal(g196,g202)
    c: Equal(g195,g199)
    c: DistanceX(g195,g199) = 4
    c: Coincident(g203,g204)
    c: Coincident(g204,g205)
    c: Coincident(g205,g206)
    c: Coincident(g206,g203)
    c: Horizontal(g203)
    c: Horizontal(g205)
    c: Vertical(g204)
    c: Vertical(g206)
    c: Equal(g196,g204) = 2
    c: Equal(g195,g203) = 30
    c: Coincident(g207,g208)
    c: Coincident(g208,g209)
    c: Coincident(g209,g210)
    c: Coincident(g210,g207)
    c: Horizontal(g207)
    c: Horizontal(g209)
    c: Vertical(g208)
    c: Vertical(g210)
    c: Equal(g204,g210)
    c: Equal(g203,g207)
    c: DistanceX(g203,g207) = 4
    c: DistanceX(g199,g203) = 4
    c: Coincident(g211,g212)
    c: Coincident(g212,g213)
    c: Coincident(g213,g214)
    c: Coincident(g214,g211)
    c: Horizontal(g211)
    c: Horizontal(g213)
    c: Vertical(g212)
    c: Vertical(g214)
    c: Equal(g208,g212)
    c: DistanceX(g207,g211) = 4
    c: Coincident(g215,g216)
    c: Coincident(g216,g217)
    c: Coincident(g217,g218)
    c: Coincident(g218,g215)
    c: Horizontal(g215)
    c: Horizontal(g217)
    c: Vertical(g216)
    c: Vertical(g218)
    c: Equal(g196,g216) = 2
    c: Equal(g195,g215) = 30
    c: Coincident(g219,g220)
    c: Coincident(g220,g221)
    c: Coincident(g221,g222)
    c: Coincident(g222,g219)
    c: Horizontal(g219)
    c: Horizontal(g221)
    c: Vertical(g220)
    c: Vertical(g222)
    c: Equal(g216,g222)
    c: Equal(g215,g219)
    c: DistanceX(g215,g219) = 4
    c: Coincident(g223,g224)
    c: Coincident(g224,g225)
    c: Coincident(g225,g226)
    c: Coincident(g226,g223)
    c: Horizontal(g223)
    c: Horizontal(g225)
    c: Vertical(g224)
    c: Vertical(g226)
    c: Equal(g216,g224) = 2
    c: Equal(g215,g223) = 30
    c: Coincident(g227,g228)
    c: Coincident(g228,g229)
    c: Coincident(g229,g230)
    c: Coincident(g230,g227)
    c: Horizontal(g227)
    c: Horizontal(g229)
    c: Vertical(g228)
    c: Vertical(g230)
    c: Equal(g224,g230)
    c: Equal(g223,g227)
    c: DistanceX(g223,g227) = 4
    c: DistanceX(g219,g223) = 4
    c: DistanceY(g223,g227) = 0
    c: DistanceY(g223,g219) = 0
    c: DistanceY(g219,g215) = 0
    c: DistanceY(g227,g208) = 3
    c: Coincident(g231,g232)
    c: Coincident(g232,g233)
    c: Coincident(g233,g234)
    c: Coincident(g234,g231)
    c: Horizontal(g231)
    c: Horizontal(g233)
    c: Vertical(g232)
    c: Vertical(g234)
    c: Equal(g218,g232)
    c: DistanceY(g231,g215) = 0
    c: DistanceX(g232,g217) = 4
    c: DistanceY(g195,g199) = 0
    c: DistanceY(g199,g203) = 0
    c: DistanceY(g203,g207) = 0
    c: DistanceY(g207,g211) = 0
    c: Coincident(g235,g236)
    c: Coincident(g236,g237)
    c: Coincident(g237,g238)
    c: Coincident(g238,g235)
    c: Horizontal(g235)
    c: Horizontal(g237)
    c: Vertical(g236)
    c: Vertical(g238)
    c: Coincident(g239,g240)
    c: Coincident(g240,g241)
    c: Coincident(g241,g242)
    c: Coincident(g242,g239)
    c: Horizontal(g239)
    c: Horizontal(g241)
    c: Vertical(g240)
    c: Vertical(g242)
    c: Equal(g236,g242)
    c: Equal(g235,g239)
    c: DistanceX(g235,g239) = 4
    c: Coincident(g243,g244)
    c: Coincident(g244,g245)
    c: Coincident(g245,g246)
    c: Coincident(g246,g243)
    c: Horizontal(g243)
    c: Horizontal(g245)
    c: Vertical(g244)
    c: Vertical(g246)
    c: Equal(g236,g244) = 2
    c: Equal(g235,g243) = 30
    c: Coincident(g247,g248)
    c: Coincident(g248,g249)
    c: Coincident(g249,g250)
    c: Coincident(g250,g247)
    c: Horizontal(g247)
    c: Horizontal(g249)
    c: Vertical(g248)
    c: Vertical(g250)
    c: Equal(g244,g250)
    c: Equal(g243,g247)
    c: DistanceX(g243,g247) = 4
    c: DistanceX(g239,g243) = 4
    c: Coincident(g251,g252)
    c: Coincident(g252,g253)
    c: Coincident(g253,g254)
    c: Coincident(g254,g251)
    c: Horizontal(g251)
    c: Horizontal(g253)
    c: Vertical(g252)
    c: Vertical(g254)
    c: Equal(g248,g252)
    c: DistanceX(g247,g251) = 4
    c: Coincident(g255,g256)
    c: Coincident(g256,g257)
    c: Coincident(g257,g258)
    c: Coincident(g258,g255)
    c: Horizontal(g255)
    c: Horizontal(g257)
    c: Vertical(g256)
    c: Vertical(g258)
    c: Equal(g236,g256) = 2
    c: Equal(g235,g255) = 30
    c: Coincident(g259,g260)
    c: Coincident(g260,g261)
    c: Coincident(g261,g262)
    c: Coincident(g262,g259)
    c: Horizontal(g259)
    c: Horizontal(g261)
    c: Vertical(g260)
    c: Vertical(g262)
    c: Equal(g256,g262)
    c: Equal(g255,g259)
    c: DistanceX(g255,g259) = 4
    c: Coincident(g263,g264)
    c: Coincident(g264,g265)
    c: Coincident(g265,g266)
    c: Coincident(g266,g263)
    c: Horizontal(g263)
    c: Horizontal(g265)
    c: Vertical(g264)
    c: Vertical(g266)
    c: Equal(g256,g264) = 2
    c: Equal(g255,g263) = 30
    c: Coincident(g267,g268)
    c: Coincident(g268,g269)
    c: Coincident(g269,g270)
    c: Coincident(g270,g267)
    c: Horizontal(g267)
    c: Horizontal(g269)
    c: Vertical(g268)
    c: Vertical(g270)
    c: Equal(g264,g270)
    c: Equal(g263,g267)
    c: DistanceX(g263,g267) = 4
    c: DistanceX(g259,g263) = 4
    c: DistanceY(g263,g267) = 0
    c: DistanceY(g263,g259) = 0
    c: DistanceY(g259,g255) = 0
    c: DistanceY(g267,g248) = 3
    c: Coincident(g271,g272)
    c: Coincident(g272,g273)
    c: Coincident(g273,g274)
    c: Coincident(g274,g271)
    c: Horizontal(g271)
    c: Horizontal(g273)
    c: Vertical(g272)
    c: Vertical(g274)
    c: Equal(g258,g272)
    c: DistanceY(g271,g255) = 0
    c: DistanceX(g272,g257) = 4
    c: Coincident(g275,g276)
    c: Coincident(g276,g277)
    c: Coincident(g277,g278)
    c: Coincident(g278,g275)
    c: Horizontal(g275)
    c: Horizontal(g277)
    c: Vertical(g276)
    c: Vertical(g278)
    c: Equal(g236,g276) = 2
    c: Equal(g235,g275) = 30
    c: Coincident(g279,g280)
    c: Coincident(g280,g281)
    c: Coincident(g281,g282)
    c: Coincident(g282,g279)
    c: Horizontal(g279)
    c: Horizontal(g281)
    c: Vertical(g280)
    c: Vertical(g282)
    c: Equal(g276,g282)
    c: Equal(g275,g279)
    c: DistanceX(g275,g279) = 4
    c: Coincident(g283,g284)
    c: Coincident(g284,g285)
    c: Coincident(g285,g286)
    c: Coincident(g286,g283)
    c: Horizontal(g283)
    c: Horizontal(g285)
    c: Vertical(g284)
    c: Vertical(g286)
    c: Equal(g276,g284) = 2
    c: Equal(g275,g283) = 30
    c: Coincident(g287,g288)
    c: Coincident(g288,g289)
    c: Coincident(g289,g290)
    c: Coincident(g290,g287)
    c: Horizontal(g287)
    c: Horizontal(g289)
    c: Vertical(g288)
    c: Vertical(g290)
    c: Equal(g284,g290)
    c: Equal(g283,g287)
    c: DistanceX(g283,g287) = 4
    c: DistanceX(g279,g283) = 4
    c: Coincident(g291,g292)
    c: Coincident(g292,g293)
    c: Coincident(g293,g294)
    c: Coincident(g294,g291)
    c: Horizontal(g291)
    c: Horizontal(g293)
    c: Vertical(g292)
    c: Vertical(g294)
    c: Equal(g288,g292)
    c: DistanceX(g287,g291) = 4
    c: Coincident(g295,g296)
    c: Coincident(g296,g297)
    c: Coincident(g297,g298)
    c: Coincident(g298,g295)
    c: Horizontal(g295)
    c: Horizontal(g297)
    c: Vertical(g296)
    c: Vertical(g298)
    c: Equal(g276,g296) = 2
    c: Equal(g275,g295) = 30
    c: Coincident(g299,g300)
    c: Coincident(g300,g301)
    c: Coincident(g301,g302)
    c: Coincident(g302,g299)
    c: Horizontal(g299)
    c: Horizontal(g301)
    c: Vertical(g300)
    c: Vertical(g302)
    c: Equal(g296,g302)
    c: Equal(g295,g299)
    c: DistanceX(g295,g299) = 4
    c: Coincident(g303,g304)
    c: Coincident(g304,g305)
    c: Coincident(g305,g306)
    c: Coincident(g306,g303)
    c: Horizontal(g303)
    c: Horizontal(g305)
    c: Vertical(g304)
    c: Vertical(g306)
    c: Equal(g296,g304) = 2
    c: Equal(g295,g303) = 30
    c: Coincident(g307,g308)
    c: Coincident(g308,g309)
    c: Coincident(g309,g310)
    c: Coincident(g310,g307)
    c: Horizontal(g307)
    c: Horizontal(g309)
    c: Vertical(g308)
    c: Vertical(g310)
    c: Equal(g304,g310)
    c: Equal(g303,g307)
    c: DistanceX(g303,g307) = 4
    c: DistanceX(g299,g303) = 4
    c: DistanceY(g303,g307) = 0
    c: DistanceY(g303,g299) = 0
    c: DistanceY(g299,g295) = 0
    c: DistanceY(g307,g288) = 3
    c: Coincident(g311,g312)
    c: Coincident(g312,g313)
    c: Coincident(g313,g314)
    c: Coincident(g314,g311)
    c: Horizontal(g311)
    c: Horizontal(g313)
    c: Vertical(g312)
    c: Vertical(g314)
    c: Equal(g298,g312)
    c: DistanceY(g311,g295) = 0
    c: DistanceX(g312,g297) = 4
    c: DistanceY(g275,g279) = 0
    c: DistanceY(g279,g283) = 0
    c: DistanceY(g283,g287) = 0
    c: DistanceY(g287,g291) = 0
    c: DistanceY(g275,g273) = 3
    c: DistanceY(g239,g235) = 0
    c: DistanceY(g243,g239) = 0
    c: DistanceY(g247,g243) = 0
    c: DistanceY(g247,g251) = 0
    c: DistanceY(g235,g233) = 3
    c: PointOnObject(g314,g2)
    c: Equal(g272,g232)
    c: PointOnObject(g195,g2)
    c: PointOnObject(g231,g2)
    c: PointOnObject(g235,g2)
    c: PointOnObject(g271,g2)
    c: PointOnObject(g275,g2)
    c: PointOnObject(g211,g0)
    c: PointOnObject(g227,g0)
    c: PointOnObject(g251,g0)
    c: PointOnObject(g267,g0)
    c: PointOnObject(g291,g0)
    c: PointOnObject(g307,g0)
    c: Equal(g195,g157)
    c: Equal(g235,g155)
    c: DistanceY(g195,g177) = 3
    c: Equal(g196,g192)
    c: Coincident(g315,g316)
    c: Coincident(g316,g317)
    c: Coincident(g317,g318)
    c: Coincident(g318,g315)
    c: Horizontal(g315)
    c: Horizontal(g317)
    c: Vertical(g316)
    c: Vertical(g318)
    c: Coincident(g319,g320)
    c: Coincident(g320,g321)
    c: Coincident(g321,g322)
    c: Coincident(g322,g319)
    c: Horizontal(g319)
    c: Horizontal(g321)
    c: Vertical(g320)
    c: Vertical(g322)
    c: Equal(g316,g322)
    c: Equal(g315,g319)
    c: DistanceX(g315,g319) = 4
    c: Coincident(g323,g324)
    c: Coincident(g324,g325)
    c: Coincident(g325,g326)
    c: Coincident(g326,g323)
    c: Horizontal(g323)
    c: Horizontal(g325)
    c: Vertical(g324)
    c: Vertical(g326)
    c: Equal(g316,g324) = 2
    c: Equal(g315,g323) = 30
    c: Coincident(g327,g328)
    c: Coincident(g328,g329)
    c: Coincident(g329,g330)
    c: Coincident(g330,g327)
    c: Horizontal(g327)
    c: Horizontal(g329)
    c: Vertical(g328)
    c: Vertical(g330)
    c: Equal(g324,g330)
    c: Equal(g323,g327)
    c: DistanceX(g323,g327) = 4
    c: DistanceX(g319,g323) = 4
    c: Coincident(g331,g332)
    c: Coincident(g332,g333)
    c: Coincident(g333,g334)
    c: Coincident(g334,g331)
    c: Horizontal(g331)
    c: Horizontal(g333)
    c: Vertical(g332)
    c: Vertical(g334)
    c: Equal(g328,g332)
    c: DistanceX(g327,g331) = 4
    c: Coincident(g335,g336)
    c: Coincident(g336,g337)
    c: Coincident(g337,g338)
    c: Coincident(g338,g335)
    c: Horizontal(g335)
    c: Horizontal(g337)
    c: Vertical(g336)
    c: Vertical(g338)
    c: Equal(g316,g336) = 2
    c: Equal(g315,g335) = 30
    c: Coincident(g339,g340)
    c: Coincident(g340,g341)
    c: Coincident(g341,g342)
    c: Coincident(g342,g339)
    c: Horizontal(g339)
    c: Horizontal(g341)
    c: Vertical(g340)
    c: Vertical(g342)
    c: Equal(g336,g342)
    c: Equal(g335,g339)
    c: DistanceX(g335,g339) = 4
    c: Coincident(g343,g344)
    c: Coincident(g344,g345)
    c: Coincident(g345,g346)
    c: Coincident(g346,g343)
    c: Horizontal(g343)
    c: Horizontal(g345)
    c: Vertical(g344)
    c: Vertical(g346)
    c: Equal(g336,g344) = 2
    c: Equal(g335,g343) = 30
    c: Coincident(g347,g348)
    c: Coincident(g348,g349)
    c: Coincident(g349,g350)
    c: Coincident(g350,g347)
    c: Horizontal(g347)
    c: Horizontal(g349)
    c: Vertical(g348)
    c: Vertical(g350)
    c: Equal(g344,g350)
    c: Equal(g343,g347)
    c: DistanceX(g343,g347) = 4
    c: DistanceX(g339,g343) = 4
    c: DistanceY(g343,g347) = 0
    c: DistanceY(g343,g339) = 0
    c: DistanceY(g339,g335) = 0
    c: DistanceY(g347,g328) = 3
    c: Coincident(g351,g352)
    c: Coincident(g352,g353)
    c: Coincident(g353,g354)
    c: Coincident(g354,g351)
    c: Horizontal(g351)
    c: Horizontal(g353)
    c: Vertical(g352)
    c: Vertical(g354)
    c: Equal(g338,g352)
    c: DistanceY(g351,g335) = 0
    c: DistanceX(g352,g337) = 4
    c: DistanceY(g315,g319) = 0
    c: DistanceY(g319,g323) = 0
    c: DistanceY(g323,g327) = 0
    c: DistanceY(g327,g331) = 0
    c: Coincident(g355,g356)
    c: Coincident(g356,g357)
    c: Coincident(g357,g358)
    c: Coincident(g358,g355)
    c: Horizontal(g355)
    c: Horizontal(g357)
    c: Vertical(g356)
    c: Vertical(g358)
    c: Coincident(g359,g360)
    c: Coincident(g360,g361)
    c: Coincident(g361,g362)
    c: Coincident(g362,g359)
    c: Horizontal(g359)
    c: Horizontal(g361)
    c: Vertical(g360)
    c: Vertical(g362)
    c: Equal(g356,g362)
    c: Equal(g355,g359)
    c: DistanceX(g355,g359) = 4
    c: Coincident(g363,g364)
    c: Coincident(g364,g365)
    c: Coincident(g365,g366)
    c: Coincident(g366,g363)
    c: Horizontal(g363)
    c: Horizontal(g365)
    c: Vertical(g364)
    c: Vertical(g366)
    c: Equal(g356,g364) = 2
    c: Equal(g355,g363) = 30
    c: Coincident(g367,g368)
    c: Coincident(g368,g369)
    c: Coincident(g369,g370)
    c: Coincident(g370,g367)
    c: Horizontal(g367)
    c: Horizontal(g369)
    c: Vertical(g368)
    c: Vertical(g370)
    c: Equal(g364,g370)
    c: Equal(g363,g367)
    c: DistanceX(g363,g367) = 4
    c: DistanceX(g359,g363) = 4
    c: Coincident(g371,g372)
    c: Coincident(g372,g373)
    c: Coincident(g373,g374)
    c: Coincident(g374,g371)
    c: Horizontal(g371)
    c: Horizontal(g373)
    c: Vertical(g372)
    c: Vertical(g374)
    c: Equal(g368,g372)
    c: DistanceX(g367,g371) = 4
    c: Coincident(g375,g376)
    c: Coincident(g376,g377)
    c: Coincident(g377,g378)
    c: Coincident(g378,g375)
    c: Horizontal(g375)
    c: Horizontal(g377)
    c: Vertical(g376)
    c: Vertical(g378)
    c: Equal(g356,g376) = 2
    c: Equal(g355,g375) = 30
    c: Coincident(g379,g380)
    c: Coincident(g380,g381)
    c: Coincident(g381,g382)
    c: Coincident(g382,g379)
    c: Horizontal(g379)
    c: Horizontal(g381)
    c: Vertical(g380)
    c: Vertical(g382)
    c: Equal(g376,g382)
    c: Equal(g375,g379)
    c: DistanceX(g375,g379) = 4
    c: Coincident(g383,g384)
    c: Coincident(g384,g385)
    c: Coincident(g385,g386)
    c: Coincident(g386,g383)
    c: Horizontal(g383)
    c: Horizontal(g385)
    c: Vertical(g384)
    c: Vertical(g386)
    c: Equal(g376,g384) = 2
    c: Equal(g375,g383) = 30
    c: Coincident(g387,g388)
    c: Coincident(g388,g389)
    c: Coincident(g389,g390)
    c: Coincident(g390,g387)
    c: Horizontal(g387)
    c: Horizontal(g389)
    c: Vertical(g388)
    c: Vertical(g390)
    c: Equal(g384,g390)
    c: Equal(g383,g387)
    c: DistanceX(g383,g387) = 4
    c: DistanceX(g379,g383) = 4
    c: DistanceY(g383,g387) = 0
    c: DistanceY(g383,g379) = 0
    c: DistanceY(g379,g375) = 0
    c: DistanceY(g387,g368) = 3
    c: Coincident(g391,g392)
    c: Coincident(g392,g393)
    c: Coincident(g393,g394)
    c: Coincident(g394,g391)
    c: Horizontal(g391)
    c: Horizontal(g393)
    c: Vertical(g392)
    c: Vertical(g394)
    c: Equal(g378,g392)
    c: DistanceY(g391,g375) = 0
    c: DistanceX(g392,g377) = 4
    c: Coincident(g395,g396)
    c: Coincident(g396,g397)
    c: Coincident(g397,g398)
    c: Coincident(g398,g395)
    c: Horizontal(g395)
    c: Horizontal(g397)
    c: Vertical(g396)
    c: Vertical(g398)
    c: Equal(g356,g396) = 2
    c: Equal(g355,g395) = 30
    c: Coincident(g399,g400)
    c: Coincident(g400,g401)
    c: Coincident(g401,g402)
    c: Coincident(g402,g399)
    c: Horizontal(g399)
    c: Horizontal(g401)
    c: Vertical(g400)
    c: Vertical(g402)
    c: Equal(g396,g402)
    c: Equal(g395,g399)
    c: DistanceX(g395,g399) = 4
    c: Coincident(g403,g404)
    c: Coincident(g404,g405)
    c: Coincident(g405,g406)
    c: Coincident(g406,g403)
    c: Horizontal(g403)
    c: Horizontal(g405)
    c: Vertical(g404)
    c: Vertical(g406)
    c: Equal(g396,g404) = 2
    c: Equal(g395,g403) = 30
    c: Coincident(g407,g408)
    c: Coincident(g408,g409)
    c: Coincident(g409,g410)
    c: Coincident(g410,g407)
    c: Horizontal(g407)
    c: Horizontal(g409)
    c: Vertical(g408)
    c: Vertical(g410)
    c: Equal(g404,g410)
    c: Equal(g403,g407)
    c: DistanceX(g403,g407) = 4
    c: DistanceX(g399,g403) = 4
    c: Coincident(g411,g412)
    c: Coincident(g412,g413)
    c: Coincident(g413,g414)
    c: Coincident(g414,g411)
    c: Horizontal(g411)
    c: Horizontal(g413)
    c: Vertical(g412)
    c: Vertical(g414)
    c: Equal(g408,g412)
    c: DistanceX(g407,g411) = 4
    c: Coincident(g415,g416)
    c: Coincident(g416,g417)
    c: Coincident(g417,g418)
    c: Coincident(g418,g415)
    c: Horizontal(g415)
    c: Horizontal(g417)
    c: Vertical(g416)
    c: Vertical(g418)
    c: Equal(g396,g416) = 2
    c: Equal(g395,g415) = 30
    c: Coincident(g419,g420)
    c: Coincident(g420,g421)
    c: Coincident(g421,g422)
    c: Coincident(g422,g419)
    c: Horizontal(g419)
    c: Horizontal(g421)
    c: Vertical(g420)
    c: Vertical(g422)
    c: Equal(g416,g422)
    c: Equal(g415,g419)
    c: DistanceX(g415,g419) = 4
    c: Coincident(g423,g424)
    c: Coincident(g424,g425)
    c: Coincident(g425,g426)
    c: Coincident(g426,g423)
    c: Horizontal(g423)
    c: Horizontal(g425)
    c: Vertical(g424)
    c: Vertical(g426)
    c: Equal(g416,g424) = 2
    c: Equal(g415,g423) = 30
    c: Coincident(g427,g428)
    c: Coincident(g428,g429)
    c: Coincident(g429,g430)
    c: Coincident(g430,g427)
    c: Horizontal(g427)
    c: Horizontal(g429)
    c: Vertical(g428)
    c: Vertical(g430)
    c: Equal(g424,g430)
    c: Equal(g423,g427)
    c: DistanceX(g423,g427) = 4
    c: DistanceX(g419,g423) = 4
    c: DistanceY(g423,g427) = 0
    c: DistanceY(g423,g419) = 0
    c: DistanceY(g419,g415) = 0
    c: DistanceY(g427,g408) = 3
    c: Coincident(g431,g432)
    c: Coincident(g432,g433)
    c: Coincident(g433,g434)
    c: Coincident(g434,g431)
    c: Horizontal(g431)
    c: Horizontal(g433)
    c: Vertical(g432)
    c: Vertical(g434)
    c: Equal(g418,g432)
    c: DistanceY(g431,g415) = 0
    c: DistanceX(g432,g417) = 4
    c: DistanceY(g395,g399) = 0
    c: DistanceY(g399,g403) = 0
    c: DistanceY(g403,g407) = 0
    c: DistanceY(g407,g411) = 0
    c: DistanceY(g395,g393) = 3
    c: DistanceY(g359,g355) = 0
    c: DistanceY(g363,g359) = 0
    c: DistanceY(g367,g363) = 0
    c: DistanceY(g367,g371) = 0
    c: DistanceY(g355,g353) = 3
    c: Coincident(g435,g436)
    c: Coincident(g436,g437)
    c: Coincident(g437,g438)
    c: Coincident(g438,g435)
    c: Horizontal(g435)
    c: Horizontal(g437)
    c: Vertical(g436)
    c: Vertical(g438)
    c: Coincident(g439,g440)
    c: Coincident(g440,g441)
    c: Coincident(g441,g442)
    c: Coincident(g442,g439)
    c: Horizontal(g439)
    c: Horizontal(g441)
    c: Vertical(g440)
    c: Vertical(g442)
    c: Equal(g436,g442)
    c: Equal(g435,g439)
    c: DistanceX(g435,g439) = 4
    c: Coincident(g443,g444)
    c: Coincident(g444,g445)
    c: Coincident(g445,g446)
    c: Coincident(g446,g443)
    c: Horizontal(g443)
    c: Horizontal(g445)
    c: Vertical(g444)
    c: Vertical(g446)
    c: Equal(g436,g444) = 2
    c: Equal(g435,g443) = 30
    c: Coincident(g447,g448)
    c: Coincident(g448,g449)
    c: Coincident(g449,g450)
    c: Coincident(g450,g447)
    c: Horizontal(g447)
    c: Horizontal(g449)
    c: Vertical(g448)
    c: Vertical(g450)
    c: Equal(g444,g450)
    c: Equal(g443,g447)
    c: DistanceX(g443,g447) = 4
    c: DistanceX(g439,g443) = 4
    c: Coincident(g451,g452)
    c: Coincident(g452,g453)
    c: Coincident(g453,g454)
    c: Coincident(g454,g451)
    c: Horizontal(g451)
    c: Horizontal(g453)
    c: Vertical(g452)
    c: Vertical(g454)
    c: Equal(g448,g452)
    c: DistanceX(g447,g451) = 4
    c: Coincident(g455,g456)
    c: Coincident(g456,g457)
    c: Coincident(g457,g458)
    c: Coincident(g458,g455)
    c: Horizontal(g455)
    c: Horizontal(g457)
    c: Vertical(g456)
    c: Vertical(g458)
    c: Equal(g436,g456) = 2
    c: Equal(g435,g455) = 30
    c: Coincident(g459,g460)
    c: Coincident(g460,g461)
    c: Coincident(g461,g462)
    c: Coincident(g462,g459)
    c: Horizontal(g459)
    c: Horizontal(g461)
    c: Vertical(g460)
    c: Vertical(g462)
    c: Equal(g456,g462)
    c: Equal(g455,g459)
    c: DistanceX(g455,g459) = 4
    c: Coincident(g463,g464)
    c: Coincident(g464,g465)
    c: Coincident(g465,g466)
    c: Coincident(g466,g463)
    c: Horizontal(g463)
    c: Horizontal(g465)
    c: Vertical(g464)
    c: Vertical(g466)
    c: Equal(g456,g464) = 2
    c: Equal(g455,g463) = 30
    c: Coincident(g467,g468)
    c: Coincident(g468,g469)
    c: Coincident(g469,g470)
    c: Coincident(g470,g467)
    c: Horizontal(g467)
    c: Horizontal(g469)
    c: Vertical(g468)
    c: Vertical(g470)
    c: Equal(g464,g470)
    c: Equal(g463,g467)
    c: DistanceX(g463,g467) = 4
    c: DistanceX(g459,g463) = 4
    c: DistanceY(g463,g467) = 0
    c: DistanceY(g463,g459) = 0
    c: DistanceY(g459,g455) = 0
    c: DistanceY(g467,g448) = 3
    c: Coincident(g471,g472)
    c: Coincident(g472,g473)
    c: Coincident(g473,g474)
    c: Coincident(g474,g471)
    c: Horizontal(g471)
    c: Horizontal(g473)
    c: Vertical(g472)
    c: Vertical(g474)
    c: Equal(g458,g472)
    c: DistanceY(g471,g455) = 0
    c: DistanceX(g472,g457) = 4
    c: DistanceY(g435,g439) = 0
    c: DistanceY(g439,g443) = 0
    c: DistanceY(g443,g447) = 0
    c: DistanceY(g447,g451) = 0
    c: Coincident(g475,g476)
    c: Coincident(g476,g477)
    c: Coincident(g477,g478)
    c: Coincident(g478,g475)
    c: Horizontal(g475)
    c: Horizontal(g477)
    c: Vertical(g476)
    c: Vertical(g478)
    c: Coincident(g479,g480)
    c: Coincident(g480,g481)
    c: Coincident(g481,g482)
    c: Coincident(g482,g479)
    c: Horizontal(g479)
    c: Horizontal(g481)
    c: Vertical(g480)
    c: Vertical(g482)
    c: Equal(g476,g482)
    c: Equal(g475,g479)
    c: DistanceX(g475,g479) = 4
    c: Coincident(g483,g484)
    c: Coincident(g484,g485)
    c: Coincident(g485,g486)
    c: Coincident(g486,g483)
    c: Horizontal(g483)
    c: Horizontal(g485)
    c: Vertical(g484)
    c: Vertical(g486)
    c: Equal(g476,g484) = 2
    c: Equal(g475,g483) = 30
    c: Coincident(g487,g488)
    c: Coincident(g488,g489)
    c: Coincident(g489,g490)
    c: Coincident(g490,g487)
    c: Horizontal(g487)
    c: Horizontal(g489)
    c: Vertical(g488)
    c: Vertical(g490)
    c: Equal(g484,g490)
    c: Equal(g483,g487)
    c: DistanceX(g483,g487) = 4
    c: DistanceX(g479,g483) = 4
    c: Coincident(g491,g492)
    c: Coincident(g492,g493)
    c: Coincident(g493,g494)
    c: Coincident(g494,g491)
    c: Horizontal(g491)
    c: Horizontal(g493)
    c: Vertical(g492)
    c: Vertical(g494)
    c: Equal(g488,g492)
    c: DistanceX(g487,g491) = 4
    c: Coincident(g495,g496)
    c: Coincident(g496,g497)
    c: Coincident(g497,g498)
    c: Coincident(g498,g495)
    c: Horizontal(g495)
    c: Horizontal(g497)
    c: Vertical(g496)
    c: Vertical(g498)
    c: Equal(g476,g496) = 2
    c: Equal(g475,g495) = 30
    c: Coincident(g499,g500)
    c: Coincident(g500,g501)
    c: Coincident(g501,g502)
    c: Coincident(g502,g499)
    c: Horizontal(g499)
    c: Horizontal(g501)
    c: Vertical(g500)
    c: Vertical(g502)
    c: Equal(g496,g502)
    c: Equal(g495,g499)
    c: DistanceX(g495,g499) = 4
    c: Coincident(g503,g504)
    c: Coincident(g504,g505)
    c: Coincident(g505,g506)
    c: Coincident(g506,g503)
    c: Horizontal(g503)
    c: Horizontal(g505)
    c: Vertical(g504)
    c: Vertical(g506)
    c: Equal(g496,g504) = 2
    c: Equal(g495,g503) = 30
    c: Coincident(g507,g508)
    c: Coincident(g508,g509)
    c: Coincident(g509,g510)
    c: Coincident(g510,g507)
    c: Horizontal(g507)
    c: Horizontal(g509)
    c: Vertical(g508)
    c: Vertical(g510)
    c: Equal(g504,g510)
    c: Equal(g503,g507)
    c: DistanceX(g503,g507) = 4
    c: DistanceX(g499,g503) = 4
    c: DistanceY(g503,g507) = 0
    c: DistanceY(g503,g499) = 0
    c: DistanceY(g499,g495) = 0
    c: DistanceY(g507,g488) = 3
    c: Coincident(g511,g512)
    c: Coincident(g512,g513)
    c: Coincident(g513,g514)
    c: Coincident(g514,g511)
    c: Horizontal(g511)
    c: Horizontal(g513)
    c: Vertical(g512)
    c: Vertical(g514)
    c: Equal(g498,g512)
    c: DistanceY(g511,g495) = 0
    c: DistanceX(g512,g497) = 4
    c: Coincident(g515,g516)
    c: Coincident(g516,g517)
    c: Coincident(g517,g518)
    c: Coincident(g518,g515)
    c: Horizontal(g515)
    c: Horizontal(g517)
    c: Vertical(g516)
    c: Vertical(g518)
    c: Equal(g476,g516) = 2
    c: Equal(g475,g515) = 30
    c: Coincident(g519,g520)
    c: Coincident(g520,g521)
    c: Coincident(g521,g522)
    c: Coincident(g522,g519)
    c: Horizontal(g519)
    c: Horizontal(g521)
    c: Vertical(g520)
    c: Vertical(g522)
    c: Equal(g516,g522)
    c: Equal(g515,g519)
    c: DistanceX(g515,g519) = 4
    c: Coincident(g523,g524)
    c: Coincident(g524,g525)
    c: Coincident(g525,g526)
    c: Coincident(g526,g523)
    c: Horizontal(g523)
    c: Horizontal(g525)
    c: Vertical(g524)
    c: Vertical(g526)
    c: Equal(g516,g524) = 2
    c: Equal(g515,g523) = 30
    c: Coincident(g527,g528)
    c: Coincident(g528,g529)
    c: Coincident(g529,g530)
    c: Coincident(g530,g527)
    c: Horizontal(g527)
    c: Horizontal(g529)
    c: Vertical(g528)
    c: Vertical(g530)
    c: Equal(g524,g530)
    c: Equal(g523,g527)
    c: DistanceX(g523,g527) = 4
    c: DistanceX(g519,g523) = 4
    c: Coincident(g531,g532)
    c: Coincident(g532,g533)
    c: Coincident(g533,g534)
    c: Coincident(g534,g531)
    c: Horizontal(g531)
    c: Horizontal(g533)
    c: Vertical(g532)
    c: Vertical(g534)
    c: Equal(g528,g532)
    c: DistanceX(g527,g531) = 4
    c: DistanceY(g515,g519) = 0
    c: DistanceY(g519,g523) = 0
    c: DistanceY(g523,g527) = 0
    c: DistanceY(g527,g531) = 0
    c: DistanceY(g515,g513) = 3
    c: DistanceY(g479,g475) = 0
    c: DistanceY(g483,g479) = 0
    c: DistanceY(g487,g483) = 0
    c: DistanceY(g487,g491) = 0
    c: DistanceY(g475,g473) = 3
    c: Equal(g512,g472)
    c: Equal(g435,g397)
    c: Equal(g475,g395)
    c: DistanceY(g435,g417) = 3
    c: Equal(g436,g432)
    c: DistanceY(g315,g297) = 3
    c: Equal(g316,g298)
    c: PointOnObject(g315,g2)
    c: PointOnObject(g351,g2)
    c: PointOnObject(g355,g2)
    c: PointOnObject(g391,g2)
    c: PointOnObject(g395,g2)
    c: PointOnObject(g431,g2)
    c: PointOnObject(g435,g2)
    c: PointOnObject(g471,g2)
    c: PointOnObject(g475,g2)
    c: PointOnObject(g511,g2)
    c: PointOnObject(g515,g2)
    c: PointOnObject(g333,g0)
    c: PointOnObject(g347,g0)
    c: PointOnObject(g371,g0)
    c: PointOnObject(g387,g0)
    c: PointOnObject(g411,g0)
    c: PointOnObject(g427,g0)
    c: PointOnObject(g451,g0)
    c: PointOnObject(g467,g0)
    c: PointOnObject(g491,g0)
    c: PointOnObject(g507,g0)
    c: PointOnObject(g531,g0)
    c: Equal(g351,g313)
    c: Equal(g355,g317)
    c: Equal(g352,g356)
FEATURE [PartDesign::Body] Body
  Group = -> [Sketch]
  Origin = -> Origin
